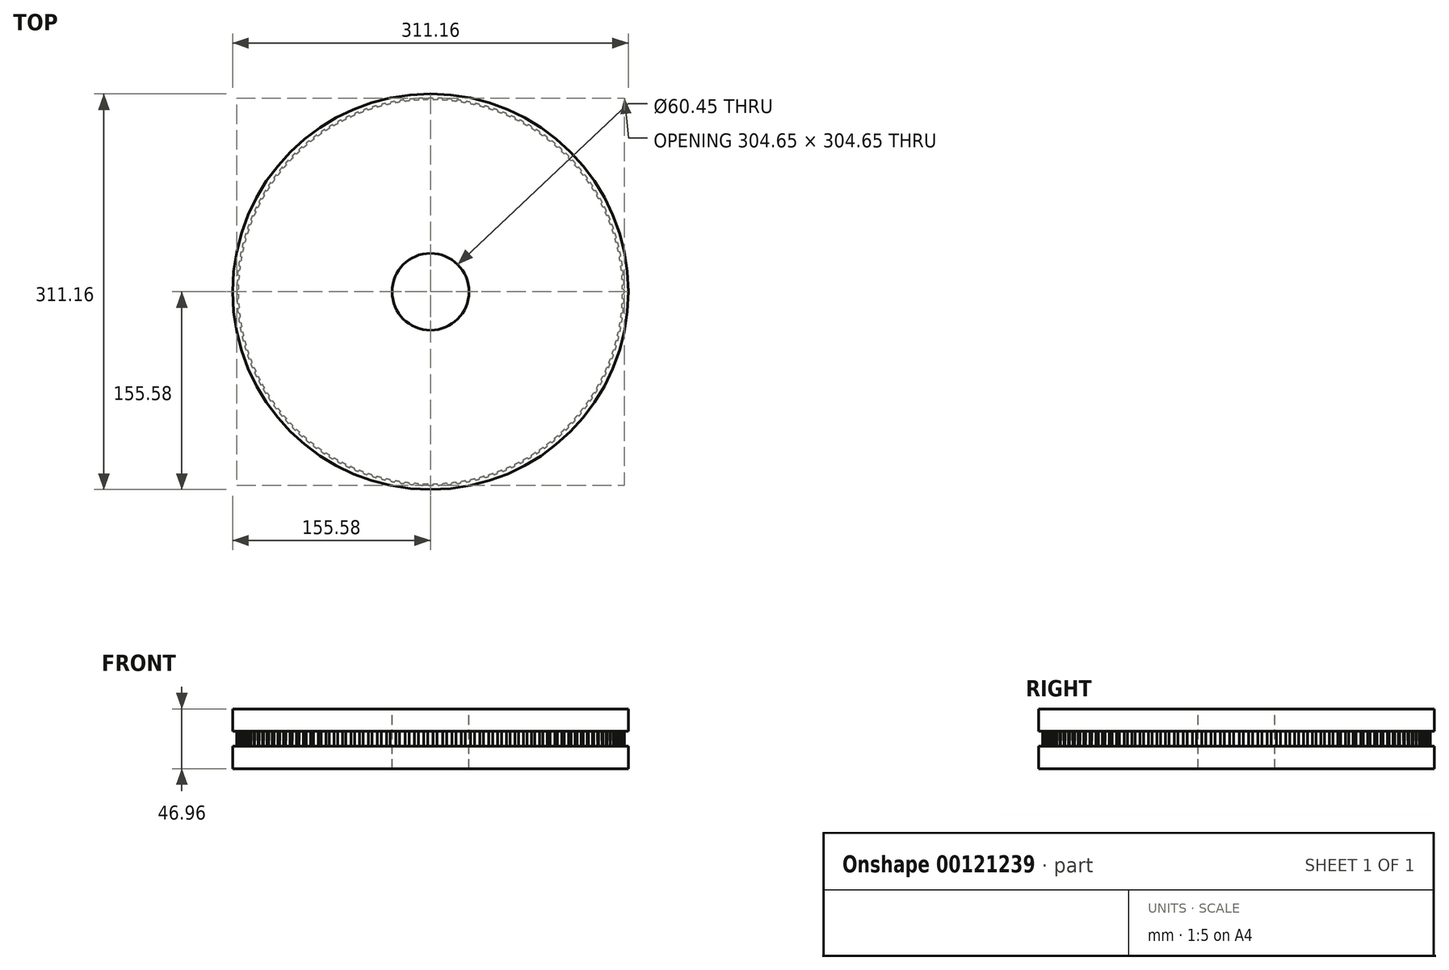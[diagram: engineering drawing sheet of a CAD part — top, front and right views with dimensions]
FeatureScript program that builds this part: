
annotation { "Feature Type Name" : "Feature", "Feature Type Description" : "" }
export const myFeature = defineFeature(function(context is Context, id is Id, definition is map)
    precondition{}
    {
        {
            var Q0;
            Q0=qCreatedBy(makeId("Top.planeOp"),FACE);
            var sketch = newSketch(context, id + "F0", { "sketchPlane" : qUnion([Q0])});
            skCircle(sketch, "E0", {"center": v(0, 0) * mm, "radius": 151 * mm});
            skSolve(sketch);
        }
        {
            var Q0;
            Q0=qSketchRegion(id+"F0",true);
            extrude(context, id + "F1", {"entities" : qUnion([Q0]), "depth" : 11.9 * mm});
        }
        {
            var Q0;
            Q0=qCreatedBy(makeId("Top.planeOp"),FACE);
            var sketch = newSketch(context, id + "F2", { "sketchPlane" : qUnion([Q0])});
            skLineSegment(sketch, "E1", {"start": v(0, -0.08) * mm, "end": v(0, 183.08) * mm, "construction": true});
            skArc(sketch, "E2", {"start": v(1.26, 152.32) * mm, "mid": v(0, 152.32) * mm, "end": v(-1.26, 152.32) * mm});
            skLineSegment(sketch, "E3", {"start": v(-1.6, 152.1) * mm, "end": v(-2.1, 151.02) * mm});
            skLineSegment(sketch, "E4", {"start": v(1.6, 152.1) * mm, "end": v(2.1, 151.02) * mm});
            skPoint(sketch, "E5.visualSharp", {"position": v(-1.5, 152.32) * mm});
            skArc(sketch, "E5.filletArc", {"start": v(-1.26, 152.32) * mm, "mid": v(-1.46, 152.26) * mm, "end": v(-1.6, 152.1) * mm});
            skPoint(sketch, "E6.visualSharp", {"position": v(1.5, 152.32) * mm});
            skArc(sketch, "E6.filletArc", {"start": v(1.6, 152.1) * mm, "mid": v(1.46, 152.26) * mm, "end": v(1.26, 152.32) * mm});
            skArc(sketch, "E7", {"start": v(-2.27, 150.9) * mm, "mid": v(-2.17, 150.94) * mm, "end": v(-2.1, 151.02) * mm});
            skArc(sketch, "E8", {"start": v(2.1, 151.02) * mm, "mid": v(2.17, 150.94) * mm, "end": v(2.27, 150.9) * mm});
            skPoint(sketch, "E9.orphan", {"position": v(2.15, 150.91) * mm});
            skArc(sketch, "E10", {"start": v(-2.27, 150.9) * mm, "mid": v(0, 150.67) * mm, "end": v(2.27, 150.9) * mm});
            skSolve(sketch);
        }
        {
            var Q0;
            Q0=makeQuery(id+"F2.imprint","IMPRINT",FACE,{"disambiguationData":[TD([[makeQuery(id+"F2.imprint","IMPRINT",EDGE,{"derivedFrom":sQuery(id+"F2.wireOp",EDGE,"E2")}),1.0]])]});
            var Q1;
            Q1=makeQuery(id+"F2.imprint","IMPRINT",FACE,{"disambiguationData":[TD([[makeQuery(id+"F2.imprint","IMPRINT",EDGE,{"derivedFrom":sQuery(id+"F2.wireOp",EDGE,"bbfa1fc5-6552-4957-9194-8f10230bb92c.0")}),1.0]])]});
            var Q2;
            Q2=makeQuery(id+"F1.opExtrude","CAP_FACE",FACE,{"disambiguationData":[OSD([sQuery(id+"F0.wireOp",EDGE,"E0")])],"isStart":false});
            extrude(context, id + "F3", {"entities" : qUnion([Q0, Q1]), "endBound" : BoundingType.UP_TO_SURFACE, "endBoundEntityFace" : qUnion([Q2]), "depth" : 25.4 * mm});
        }
        {
            var Q0;
            Q0=qCreatedBy(makeId("Front.planeOp"),FACE);
            var sketch = newSketch(context, id + "F4", { "sketchPlane" : qUnion([Q0])});
            skLineSegment(sketch, "E11", {"start": v(0, 74.48) * mm, "end": v(0, -67.78) * mm, "construction": true});
            skSolve(sketch);
        }
        {
            var Q0;
            Q0=makeQuery(id+"F3.opExtrude","SWEPT_BODY",BODY,{"disambiguationData":[OSD([sQuery(id+"F2.wireOp",EDGE,"E2"),sQuery(id+"F2.wireOp",EDGE,"E3"),sQuery(id+"F2.wireOp",EDGE,"E4"),sQuery(id+"F2.wireOp",EDGE,"E5.filletArc"),sQuery(id+"F2.wireOp",EDGE,"E6.filletArc"),sQuery(id+"F2.wireOp",EDGE,"E7"),sQuery(id+"F2.wireOp",EDGE,"E8"),sQuery(id+"F2.wireOp",EDGE,"E10")])]});
            var Q1;
            Q1=sQuery(id+"F4.wireOp",EDGE,"E11");
            circularPattern(context, id + "F5", {"entities" : qUnion([Q0]), "axis" : qUnion([Q1]), "angle" : 360 * degree, "instanceCount" : 128, "equalSpace" : true});
        }
        {
            var Q0;
            Q0=makeQuery(id+"F1.opExtrude","SWEPT_BODY",BODY,{"disambiguationData":[OSD([sQuery(id+"F0.wireOp",EDGE,"E0")])]});
            var Q1;
            Q1=makeQuery(id+"F3.opExtrude","SWEPT_BODY",BODY,{"disambiguationData":[OSD([sQuery(id+"F2.wireOp",EDGE,"E2"),sQuery(id+"F2.wireOp",EDGE,"E3"),sQuery(id+"F2.wireOp",EDGE,"E4"),sQuery(id+"F2.wireOp",EDGE,"E5.filletArc"),sQuery(id+"F2.wireOp",EDGE,"E6.filletArc"),sQuery(id+"F2.wireOp",EDGE,"E7"),sQuery(id+"F2.wireOp",EDGE,"E8"),sQuery(id+"F2.wireOp",EDGE,"E10")])]});
            var Q2;
            Q2=makeQuery(id+"F5.opPattern","COPY",BODY,{"derivedFrom":makeQuery(id+"F3.opExtrude","SWEPT_BODY",BODY,{"disambiguationData":[OSD([sQuery(id+"F2.wireOp",EDGE,"E2"),sQuery(id+"F2.wireOp",EDGE,"E3"),sQuery(id+"F2.wireOp",EDGE,"E4"),sQuery(id+"F2.wireOp",EDGE,"E5.filletArc"),sQuery(id+"F2.wireOp",EDGE,"E6.filletArc"),sQuery(id+"F2.wireOp",EDGE,"E7"),sQuery(id+"F2.wireOp",EDGE,"E8"),sQuery(id+"F2.wireOp",EDGE,"E10")])]}),"instanceName":"1"});
            var Q3;
            Q3=makeQuery(id+"F5.opPattern","COPY",BODY,{"derivedFrom":makeQuery(id+"F3.opExtrude","SWEPT_BODY",BODY,{"disambiguationData":[OSD([sQuery(id+"F2.wireOp",EDGE,"E2"),sQuery(id+"F2.wireOp",EDGE,"E3"),sQuery(id+"F2.wireOp",EDGE,"E4"),sQuery(id+"F2.wireOp",EDGE,"E5.filletArc"),sQuery(id+"F2.wireOp",EDGE,"E6.filletArc"),sQuery(id+"F2.wireOp",EDGE,"E7"),sQuery(id+"F2.wireOp",EDGE,"E8"),sQuery(id+"F2.wireOp",EDGE,"E10")])]}),"instanceName":"2"});
            var Q4;
            Q4=makeQuery(id+"F5.opPattern","COPY",BODY,{"derivedFrom":makeQuery(id+"F3.opExtrude","SWEPT_BODY",BODY,{"disambiguationData":[OSD([sQuery(id+"F2.wireOp",EDGE,"E2"),sQuery(id+"F2.wireOp",EDGE,"E3"),sQuery(id+"F2.wireOp",EDGE,"E4"),sQuery(id+"F2.wireOp",EDGE,"E5.filletArc"),sQuery(id+"F2.wireOp",EDGE,"E6.filletArc"),sQuery(id+"F2.wireOp",EDGE,"E7"),sQuery(id+"F2.wireOp",EDGE,"E8"),sQuery(id+"F2.wireOp",EDGE,"E10")])]}),"instanceName":"3"});
            var Q5;
            Q5=makeQuery(id+"F5.opPattern","COPY",BODY,{"derivedFrom":makeQuery(id+"F3.opExtrude","SWEPT_BODY",BODY,{"disambiguationData":[OSD([sQuery(id+"F2.wireOp",EDGE,"E2"),sQuery(id+"F2.wireOp",EDGE,"E3"),sQuery(id+"F2.wireOp",EDGE,"E4"),sQuery(id+"F2.wireOp",EDGE,"E5.filletArc"),sQuery(id+"F2.wireOp",EDGE,"E6.filletArc"),sQuery(id+"F2.wireOp",EDGE,"E7"),sQuery(id+"F2.wireOp",EDGE,"E8"),sQuery(id+"F2.wireOp",EDGE,"E10")])]}),"instanceName":"4"});
            var Q6;
            Q6=makeQuery(id+"F5.opPattern","COPY",BODY,{"derivedFrom":makeQuery(id+"F3.opExtrude","SWEPT_BODY",BODY,{"disambiguationData":[OSD([sQuery(id+"F2.wireOp",EDGE,"E2"),sQuery(id+"F2.wireOp",EDGE,"E3"),sQuery(id+"F2.wireOp",EDGE,"E4"),sQuery(id+"F2.wireOp",EDGE,"E5.filletArc"),sQuery(id+"F2.wireOp",EDGE,"E6.filletArc"),sQuery(id+"F2.wireOp",EDGE,"E7"),sQuery(id+"F2.wireOp",EDGE,"E8"),sQuery(id+"F2.wireOp",EDGE,"E10")])]}),"instanceName":"5"});
            var Q7;
            Q7=makeQuery(id+"F5.opPattern","COPY",BODY,{"derivedFrom":makeQuery(id+"F3.opExtrude","SWEPT_BODY",BODY,{"disambiguationData":[OSD([sQuery(id+"F2.wireOp",EDGE,"E2"),sQuery(id+"F2.wireOp",EDGE,"E3"),sQuery(id+"F2.wireOp",EDGE,"E4"),sQuery(id+"F2.wireOp",EDGE,"E5.filletArc"),sQuery(id+"F2.wireOp",EDGE,"E6.filletArc"),sQuery(id+"F2.wireOp",EDGE,"E7"),sQuery(id+"F2.wireOp",EDGE,"E8"),sQuery(id+"F2.wireOp",EDGE,"E10")])]}),"instanceName":"6"});
            var Q8;
            Q8=makeQuery(id+"F5.opPattern","COPY",BODY,{"derivedFrom":makeQuery(id+"F3.opExtrude","SWEPT_BODY",BODY,{"disambiguationData":[OSD([sQuery(id+"F2.wireOp",EDGE,"E2"),sQuery(id+"F2.wireOp",EDGE,"E3"),sQuery(id+"F2.wireOp",EDGE,"E4"),sQuery(id+"F2.wireOp",EDGE,"E5.filletArc"),sQuery(id+"F2.wireOp",EDGE,"E6.filletArc"),sQuery(id+"F2.wireOp",EDGE,"E7"),sQuery(id+"F2.wireOp",EDGE,"E8"),sQuery(id+"F2.wireOp",EDGE,"E10")])]}),"instanceName":"7"});
            var Q9;
            Q9=makeQuery(id+"F5.opPattern","COPY",BODY,{"derivedFrom":makeQuery(id+"F3.opExtrude","SWEPT_BODY",BODY,{"disambiguationData":[OSD([sQuery(id+"F2.wireOp",EDGE,"E2"),sQuery(id+"F2.wireOp",EDGE,"E3"),sQuery(id+"F2.wireOp",EDGE,"E4"),sQuery(id+"F2.wireOp",EDGE,"E5.filletArc"),sQuery(id+"F2.wireOp",EDGE,"E6.filletArc"),sQuery(id+"F2.wireOp",EDGE,"E7"),sQuery(id+"F2.wireOp",EDGE,"E8"),sQuery(id+"F2.wireOp",EDGE,"E10")])]}),"instanceName":"8"});
            var Q10;
            Q10=makeQuery(id+"F5.opPattern","COPY",BODY,{"derivedFrom":makeQuery(id+"F3.opExtrude","SWEPT_BODY",BODY,{"disambiguationData":[OSD([sQuery(id+"F2.wireOp",EDGE,"E2"),sQuery(id+"F2.wireOp",EDGE,"E3"),sQuery(id+"F2.wireOp",EDGE,"E4"),sQuery(id+"F2.wireOp",EDGE,"E5.filletArc"),sQuery(id+"F2.wireOp",EDGE,"E6.filletArc"),sQuery(id+"F2.wireOp",EDGE,"E7"),sQuery(id+"F2.wireOp",EDGE,"E8"),sQuery(id+"F2.wireOp",EDGE,"E10")])]}),"instanceName":"9"});
            var Q11;
            Q11=makeQuery(id+"F5.opPattern","COPY",BODY,{"derivedFrom":makeQuery(id+"F3.opExtrude","SWEPT_BODY",BODY,{"disambiguationData":[OSD([sQuery(id+"F2.wireOp",EDGE,"E2"),sQuery(id+"F2.wireOp",EDGE,"E3"),sQuery(id+"F2.wireOp",EDGE,"E4"),sQuery(id+"F2.wireOp",EDGE,"E5.filletArc"),sQuery(id+"F2.wireOp",EDGE,"E6.filletArc"),sQuery(id+"F2.wireOp",EDGE,"E7"),sQuery(id+"F2.wireOp",EDGE,"E8"),sQuery(id+"F2.wireOp",EDGE,"E10")])]}),"instanceName":"10"});
            var Q12;
            Q12=makeQuery(id+"F5.opPattern","COPY",BODY,{"derivedFrom":makeQuery(id+"F3.opExtrude","SWEPT_BODY",BODY,{"disambiguationData":[OSD([sQuery(id+"F2.wireOp",EDGE,"E2"),sQuery(id+"F2.wireOp",EDGE,"E3"),sQuery(id+"F2.wireOp",EDGE,"E4"),sQuery(id+"F2.wireOp",EDGE,"E5.filletArc"),sQuery(id+"F2.wireOp",EDGE,"E6.filletArc"),sQuery(id+"F2.wireOp",EDGE,"E7"),sQuery(id+"F2.wireOp",EDGE,"E8"),sQuery(id+"F2.wireOp",EDGE,"E10")])]}),"instanceName":"11"});
            var Q13;
            Q13=makeQuery(id+"F5.opPattern","COPY",BODY,{"derivedFrom":makeQuery(id+"F3.opExtrude","SWEPT_BODY",BODY,{"disambiguationData":[OSD([sQuery(id+"F2.wireOp",EDGE,"E2"),sQuery(id+"F2.wireOp",EDGE,"E3"),sQuery(id+"F2.wireOp",EDGE,"E4"),sQuery(id+"F2.wireOp",EDGE,"E5.filletArc"),sQuery(id+"F2.wireOp",EDGE,"E6.filletArc"),sQuery(id+"F2.wireOp",EDGE,"E7"),sQuery(id+"F2.wireOp",EDGE,"E8"),sQuery(id+"F2.wireOp",EDGE,"E10")])]}),"instanceName":"12"});
            var Q14;
            Q14=makeQuery(id+"F5.opPattern","COPY",BODY,{"derivedFrom":makeQuery(id+"F3.opExtrude","SWEPT_BODY",BODY,{"disambiguationData":[OSD([sQuery(id+"F2.wireOp",EDGE,"E2"),sQuery(id+"F2.wireOp",EDGE,"E3"),sQuery(id+"F2.wireOp",EDGE,"E4"),sQuery(id+"F2.wireOp",EDGE,"E5.filletArc"),sQuery(id+"F2.wireOp",EDGE,"E6.filletArc"),sQuery(id+"F2.wireOp",EDGE,"E7"),sQuery(id+"F2.wireOp",EDGE,"E8"),sQuery(id+"F2.wireOp",EDGE,"E10")])]}),"instanceName":"13"});
            var Q15;
            Q15=makeQuery(id+"F5.opPattern","COPY",BODY,{"derivedFrom":makeQuery(id+"F3.opExtrude","SWEPT_BODY",BODY,{"disambiguationData":[OSD([sQuery(id+"F2.wireOp",EDGE,"E2"),sQuery(id+"F2.wireOp",EDGE,"E3"),sQuery(id+"F2.wireOp",EDGE,"E4"),sQuery(id+"F2.wireOp",EDGE,"E5.filletArc"),sQuery(id+"F2.wireOp",EDGE,"E6.filletArc"),sQuery(id+"F2.wireOp",EDGE,"E7"),sQuery(id+"F2.wireOp",EDGE,"E8"),sQuery(id+"F2.wireOp",EDGE,"E10")])]}),"instanceName":"14"});
            var Q16;
            Q16=makeQuery(id+"F5.opPattern","COPY",BODY,{"derivedFrom":makeQuery(id+"F3.opExtrude","SWEPT_BODY",BODY,{"disambiguationData":[OSD([sQuery(id+"F2.wireOp",EDGE,"E2"),sQuery(id+"F2.wireOp",EDGE,"E3"),sQuery(id+"F2.wireOp",EDGE,"E4"),sQuery(id+"F2.wireOp",EDGE,"E5.filletArc"),sQuery(id+"F2.wireOp",EDGE,"E6.filletArc"),sQuery(id+"F2.wireOp",EDGE,"E7"),sQuery(id+"F2.wireOp",EDGE,"E8"),sQuery(id+"F2.wireOp",EDGE,"E10")])]}),"instanceName":"15"});
            var Q17;
            Q17=makeQuery(id+"F5.opPattern","COPY",BODY,{"derivedFrom":makeQuery(id+"F3.opExtrude","SWEPT_BODY",BODY,{"disambiguationData":[OSD([sQuery(id+"F2.wireOp",EDGE,"E2"),sQuery(id+"F2.wireOp",EDGE,"E3"),sQuery(id+"F2.wireOp",EDGE,"E4"),sQuery(id+"F2.wireOp",EDGE,"E5.filletArc"),sQuery(id+"F2.wireOp",EDGE,"E6.filletArc"),sQuery(id+"F2.wireOp",EDGE,"E7"),sQuery(id+"F2.wireOp",EDGE,"E8"),sQuery(id+"F2.wireOp",EDGE,"E10")])]}),"instanceName":"16"});
            var Q18;
            Q18=makeQuery(id+"F5.opPattern","COPY",BODY,{"derivedFrom":makeQuery(id+"F3.opExtrude","SWEPT_BODY",BODY,{"disambiguationData":[OSD([sQuery(id+"F2.wireOp",EDGE,"E2"),sQuery(id+"F2.wireOp",EDGE,"E3"),sQuery(id+"F2.wireOp",EDGE,"E4"),sQuery(id+"F2.wireOp",EDGE,"E5.filletArc"),sQuery(id+"F2.wireOp",EDGE,"E6.filletArc"),sQuery(id+"F2.wireOp",EDGE,"E7"),sQuery(id+"F2.wireOp",EDGE,"E8"),sQuery(id+"F2.wireOp",EDGE,"E10")])]}),"instanceName":"17"});
            var Q19;
            Q19=makeQuery(id+"F5.opPattern","COPY",BODY,{"derivedFrom":makeQuery(id+"F3.opExtrude","SWEPT_BODY",BODY,{"disambiguationData":[OSD([sQuery(id+"F2.wireOp",EDGE,"E2"),sQuery(id+"F2.wireOp",EDGE,"E3"),sQuery(id+"F2.wireOp",EDGE,"E4"),sQuery(id+"F2.wireOp",EDGE,"E5.filletArc"),sQuery(id+"F2.wireOp",EDGE,"E6.filletArc"),sQuery(id+"F2.wireOp",EDGE,"E7"),sQuery(id+"F2.wireOp",EDGE,"E8"),sQuery(id+"F2.wireOp",EDGE,"E10")])]}),"instanceName":"18"});
            var Q20;
            Q20=makeQuery(id+"F5.opPattern","COPY",BODY,{"derivedFrom":makeQuery(id+"F3.opExtrude","SWEPT_BODY",BODY,{"disambiguationData":[OSD([sQuery(id+"F2.wireOp",EDGE,"E2"),sQuery(id+"F2.wireOp",EDGE,"E3"),sQuery(id+"F2.wireOp",EDGE,"E4"),sQuery(id+"F2.wireOp",EDGE,"E5.filletArc"),sQuery(id+"F2.wireOp",EDGE,"E6.filletArc"),sQuery(id+"F2.wireOp",EDGE,"E7"),sQuery(id+"F2.wireOp",EDGE,"E8"),sQuery(id+"F2.wireOp",EDGE,"E10")])]}),"instanceName":"19"});
            var Q21;
            Q21=makeQuery(id+"F5.opPattern","COPY",BODY,{"derivedFrom":makeQuery(id+"F3.opExtrude","SWEPT_BODY",BODY,{"disambiguationData":[OSD([sQuery(id+"F2.wireOp",EDGE,"E2"),sQuery(id+"F2.wireOp",EDGE,"E3"),sQuery(id+"F2.wireOp",EDGE,"E4"),sQuery(id+"F2.wireOp",EDGE,"E5.filletArc"),sQuery(id+"F2.wireOp",EDGE,"E6.filletArc"),sQuery(id+"F2.wireOp",EDGE,"E7"),sQuery(id+"F2.wireOp",EDGE,"E8"),sQuery(id+"F2.wireOp",EDGE,"E10")])]}),"instanceName":"20"});
            var Q22;
            Q22=makeQuery(id+"F5.opPattern","COPY",BODY,{"derivedFrom":makeQuery(id+"F3.opExtrude","SWEPT_BODY",BODY,{"disambiguationData":[OSD([sQuery(id+"F2.wireOp",EDGE,"E2"),sQuery(id+"F2.wireOp",EDGE,"E3"),sQuery(id+"F2.wireOp",EDGE,"E4"),sQuery(id+"F2.wireOp",EDGE,"E5.filletArc"),sQuery(id+"F2.wireOp",EDGE,"E6.filletArc"),sQuery(id+"F2.wireOp",EDGE,"E7"),sQuery(id+"F2.wireOp",EDGE,"E8"),sQuery(id+"F2.wireOp",EDGE,"E10")])]}),"instanceName":"21"});
            var Q23;
            Q23=makeQuery(id+"F5.opPattern","COPY",BODY,{"derivedFrom":makeQuery(id+"F3.opExtrude","SWEPT_BODY",BODY,{"disambiguationData":[OSD([sQuery(id+"F2.wireOp",EDGE,"E2"),sQuery(id+"F2.wireOp",EDGE,"E3"),sQuery(id+"F2.wireOp",EDGE,"E4"),sQuery(id+"F2.wireOp",EDGE,"E5.filletArc"),sQuery(id+"F2.wireOp",EDGE,"E6.filletArc"),sQuery(id+"F2.wireOp",EDGE,"E7"),sQuery(id+"F2.wireOp",EDGE,"E8"),sQuery(id+"F2.wireOp",EDGE,"E10")])]}),"instanceName":"22"});
            var Q24;
            Q24=makeQuery(id+"F5.opPattern","COPY",BODY,{"derivedFrom":makeQuery(id+"F3.opExtrude","SWEPT_BODY",BODY,{"disambiguationData":[OSD([sQuery(id+"F2.wireOp",EDGE,"E2"),sQuery(id+"F2.wireOp",EDGE,"E3"),sQuery(id+"F2.wireOp",EDGE,"E4"),sQuery(id+"F2.wireOp",EDGE,"E5.filletArc"),sQuery(id+"F2.wireOp",EDGE,"E6.filletArc"),sQuery(id+"F2.wireOp",EDGE,"E7"),sQuery(id+"F2.wireOp",EDGE,"E8"),sQuery(id+"F2.wireOp",EDGE,"E10")])]}),"instanceName":"23"});
            var Q25;
            Q25=makeQuery(id+"F5.opPattern","COPY",BODY,{"derivedFrom":makeQuery(id+"F3.opExtrude","SWEPT_BODY",BODY,{"disambiguationData":[OSD([sQuery(id+"F2.wireOp",EDGE,"E2"),sQuery(id+"F2.wireOp",EDGE,"E3"),sQuery(id+"F2.wireOp",EDGE,"E4"),sQuery(id+"F2.wireOp",EDGE,"E5.filletArc"),sQuery(id+"F2.wireOp",EDGE,"E6.filletArc"),sQuery(id+"F2.wireOp",EDGE,"E7"),sQuery(id+"F2.wireOp",EDGE,"E8"),sQuery(id+"F2.wireOp",EDGE,"E10")])]}),"instanceName":"24"});
            var Q26;
            Q26=makeQuery(id+"F5.opPattern","COPY",BODY,{"derivedFrom":makeQuery(id+"F3.opExtrude","SWEPT_BODY",BODY,{"disambiguationData":[OSD([sQuery(id+"F2.wireOp",EDGE,"E2"),sQuery(id+"F2.wireOp",EDGE,"E3"),sQuery(id+"F2.wireOp",EDGE,"E4"),sQuery(id+"F2.wireOp",EDGE,"E5.filletArc"),sQuery(id+"F2.wireOp",EDGE,"E6.filletArc"),sQuery(id+"F2.wireOp",EDGE,"E7"),sQuery(id+"F2.wireOp",EDGE,"E8"),sQuery(id+"F2.wireOp",EDGE,"E10")])]}),"instanceName":"25"});
            var Q27;
            Q27=makeQuery(id+"F5.opPattern","COPY",BODY,{"derivedFrom":makeQuery(id+"F3.opExtrude","SWEPT_BODY",BODY,{"disambiguationData":[OSD([sQuery(id+"F2.wireOp",EDGE,"E2"),sQuery(id+"F2.wireOp",EDGE,"E3"),sQuery(id+"F2.wireOp",EDGE,"E4"),sQuery(id+"F2.wireOp",EDGE,"E5.filletArc"),sQuery(id+"F2.wireOp",EDGE,"E6.filletArc"),sQuery(id+"F2.wireOp",EDGE,"E7"),sQuery(id+"F2.wireOp",EDGE,"E8"),sQuery(id+"F2.wireOp",EDGE,"E10")])]}),"instanceName":"26"});
            var Q28;
            Q28=makeQuery(id+"F5.opPattern","COPY",BODY,{"derivedFrom":makeQuery(id+"F3.opExtrude","SWEPT_BODY",BODY,{"disambiguationData":[OSD([sQuery(id+"F2.wireOp",EDGE,"E2"),sQuery(id+"F2.wireOp",EDGE,"E3"),sQuery(id+"F2.wireOp",EDGE,"E4"),sQuery(id+"F2.wireOp",EDGE,"E5.filletArc"),sQuery(id+"F2.wireOp",EDGE,"E6.filletArc"),sQuery(id+"F2.wireOp",EDGE,"E7"),sQuery(id+"F2.wireOp",EDGE,"E8"),sQuery(id+"F2.wireOp",EDGE,"E10")])]}),"instanceName":"27"});
            var Q29;
            Q29=makeQuery(id+"F5.opPattern","COPY",BODY,{"derivedFrom":makeQuery(id+"F3.opExtrude","SWEPT_BODY",BODY,{"disambiguationData":[OSD([sQuery(id+"F2.wireOp",EDGE,"E2"),sQuery(id+"F2.wireOp",EDGE,"E3"),sQuery(id+"F2.wireOp",EDGE,"E4"),sQuery(id+"F2.wireOp",EDGE,"E5.filletArc"),sQuery(id+"F2.wireOp",EDGE,"E6.filletArc"),sQuery(id+"F2.wireOp",EDGE,"E7"),sQuery(id+"F2.wireOp",EDGE,"E8"),sQuery(id+"F2.wireOp",EDGE,"E10")])]}),"instanceName":"28"});
            var Q30;
            Q30=makeQuery(id+"F5.opPattern","COPY",BODY,{"derivedFrom":makeQuery(id+"F3.opExtrude","SWEPT_BODY",BODY,{"disambiguationData":[OSD([sQuery(id+"F2.wireOp",EDGE,"E2"),sQuery(id+"F2.wireOp",EDGE,"E3"),sQuery(id+"F2.wireOp",EDGE,"E4"),sQuery(id+"F2.wireOp",EDGE,"E5.filletArc"),sQuery(id+"F2.wireOp",EDGE,"E6.filletArc"),sQuery(id+"F2.wireOp",EDGE,"E7"),sQuery(id+"F2.wireOp",EDGE,"E8"),sQuery(id+"F2.wireOp",EDGE,"E10")])]}),"instanceName":"29"});
            var Q31;
            Q31=makeQuery(id+"F5.opPattern","COPY",BODY,{"derivedFrom":makeQuery(id+"F3.opExtrude","SWEPT_BODY",BODY,{"disambiguationData":[OSD([sQuery(id+"F2.wireOp",EDGE,"E2"),sQuery(id+"F2.wireOp",EDGE,"E3"),sQuery(id+"F2.wireOp",EDGE,"E4"),sQuery(id+"F2.wireOp",EDGE,"E5.filletArc"),sQuery(id+"F2.wireOp",EDGE,"E6.filletArc"),sQuery(id+"F2.wireOp",EDGE,"E7"),sQuery(id+"F2.wireOp",EDGE,"E8"),sQuery(id+"F2.wireOp",EDGE,"E10")])]}),"instanceName":"30"});
            var Q32;
            Q32=makeQuery(id+"F5.opPattern","COPY",BODY,{"derivedFrom":makeQuery(id+"F3.opExtrude","SWEPT_BODY",BODY,{"disambiguationData":[OSD([sQuery(id+"F2.wireOp",EDGE,"E2"),sQuery(id+"F2.wireOp",EDGE,"E3"),sQuery(id+"F2.wireOp",EDGE,"E4"),sQuery(id+"F2.wireOp",EDGE,"E5.filletArc"),sQuery(id+"F2.wireOp",EDGE,"E6.filletArc"),sQuery(id+"F2.wireOp",EDGE,"E7"),sQuery(id+"F2.wireOp",EDGE,"E8"),sQuery(id+"F2.wireOp",EDGE,"E10")])]}),"instanceName":"31"});
            var Q33;
            Q33=makeQuery(id+"F5.opPattern","COPY",BODY,{"derivedFrom":makeQuery(id+"F3.opExtrude","SWEPT_BODY",BODY,{"disambiguationData":[OSD([sQuery(id+"F2.wireOp",EDGE,"E2"),sQuery(id+"F2.wireOp",EDGE,"E3"),sQuery(id+"F2.wireOp",EDGE,"E4"),sQuery(id+"F2.wireOp",EDGE,"E5.filletArc"),sQuery(id+"F2.wireOp",EDGE,"E6.filletArc"),sQuery(id+"F2.wireOp",EDGE,"E7"),sQuery(id+"F2.wireOp",EDGE,"E8"),sQuery(id+"F2.wireOp",EDGE,"E10")])]}),"instanceName":"32"});
            var Q34;
            Q34=makeQuery(id+"F5.opPattern","COPY",BODY,{"derivedFrom":makeQuery(id+"F3.opExtrude","SWEPT_BODY",BODY,{"disambiguationData":[OSD([sQuery(id+"F2.wireOp",EDGE,"E2"),sQuery(id+"F2.wireOp",EDGE,"E3"),sQuery(id+"F2.wireOp",EDGE,"E4"),sQuery(id+"F2.wireOp",EDGE,"E5.filletArc"),sQuery(id+"F2.wireOp",EDGE,"E6.filletArc"),sQuery(id+"F2.wireOp",EDGE,"E7"),sQuery(id+"F2.wireOp",EDGE,"E8"),sQuery(id+"F2.wireOp",EDGE,"E10")])]}),"instanceName":"33"});
            var Q35;
            Q35=makeQuery(id+"F5.opPattern","COPY",BODY,{"derivedFrom":makeQuery(id+"F3.opExtrude","SWEPT_BODY",BODY,{"disambiguationData":[OSD([sQuery(id+"F2.wireOp",EDGE,"E2"),sQuery(id+"F2.wireOp",EDGE,"E3"),sQuery(id+"F2.wireOp",EDGE,"E4"),sQuery(id+"F2.wireOp",EDGE,"E5.filletArc"),sQuery(id+"F2.wireOp",EDGE,"E6.filletArc"),sQuery(id+"F2.wireOp",EDGE,"E7"),sQuery(id+"F2.wireOp",EDGE,"E8"),sQuery(id+"F2.wireOp",EDGE,"E10")])]}),"instanceName":"34"});
            var Q36;
            Q36=makeQuery(id+"F5.opPattern","COPY",BODY,{"derivedFrom":makeQuery(id+"F3.opExtrude","SWEPT_BODY",BODY,{"disambiguationData":[OSD([sQuery(id+"F2.wireOp",EDGE,"E2"),sQuery(id+"F2.wireOp",EDGE,"E3"),sQuery(id+"F2.wireOp",EDGE,"E4"),sQuery(id+"F2.wireOp",EDGE,"E5.filletArc"),sQuery(id+"F2.wireOp",EDGE,"E6.filletArc"),sQuery(id+"F2.wireOp",EDGE,"E7"),sQuery(id+"F2.wireOp",EDGE,"E8"),sQuery(id+"F2.wireOp",EDGE,"E10")])]}),"instanceName":"35"});
            var Q37;
            Q37=makeQuery(id+"F5.opPattern","COPY",BODY,{"derivedFrom":makeQuery(id+"F3.opExtrude","SWEPT_BODY",BODY,{"disambiguationData":[OSD([sQuery(id+"F2.wireOp",EDGE,"E2"),sQuery(id+"F2.wireOp",EDGE,"E3"),sQuery(id+"F2.wireOp",EDGE,"E4"),sQuery(id+"F2.wireOp",EDGE,"E5.filletArc"),sQuery(id+"F2.wireOp",EDGE,"E6.filletArc"),sQuery(id+"F2.wireOp",EDGE,"E7"),sQuery(id+"F2.wireOp",EDGE,"E8"),sQuery(id+"F2.wireOp",EDGE,"E10")])]}),"instanceName":"36"});
            var Q38;
            Q38=makeQuery(id+"F5.opPattern","COPY",BODY,{"derivedFrom":makeQuery(id+"F3.opExtrude","SWEPT_BODY",BODY,{"disambiguationData":[OSD([sQuery(id+"F2.wireOp",EDGE,"E2"),sQuery(id+"F2.wireOp",EDGE,"E3"),sQuery(id+"F2.wireOp",EDGE,"E4"),sQuery(id+"F2.wireOp",EDGE,"E5.filletArc"),sQuery(id+"F2.wireOp",EDGE,"E6.filletArc"),sQuery(id+"F2.wireOp",EDGE,"E7"),sQuery(id+"F2.wireOp",EDGE,"E8"),sQuery(id+"F2.wireOp",EDGE,"E10")])]}),"instanceName":"37"});
            var Q39;
            Q39=makeQuery(id+"F5.opPattern","COPY",BODY,{"derivedFrom":makeQuery(id+"F3.opExtrude","SWEPT_BODY",BODY,{"disambiguationData":[OSD([sQuery(id+"F2.wireOp",EDGE,"E2"),sQuery(id+"F2.wireOp",EDGE,"E3"),sQuery(id+"F2.wireOp",EDGE,"E4"),sQuery(id+"F2.wireOp",EDGE,"E5.filletArc"),sQuery(id+"F2.wireOp",EDGE,"E6.filletArc"),sQuery(id+"F2.wireOp",EDGE,"E7"),sQuery(id+"F2.wireOp",EDGE,"E8"),sQuery(id+"F2.wireOp",EDGE,"E10")])]}),"instanceName":"38"});
            var Q40;
            Q40=makeQuery(id+"F5.opPattern","COPY",BODY,{"derivedFrom":makeQuery(id+"F3.opExtrude","SWEPT_BODY",BODY,{"disambiguationData":[OSD([sQuery(id+"F2.wireOp",EDGE,"E2"),sQuery(id+"F2.wireOp",EDGE,"E3"),sQuery(id+"F2.wireOp",EDGE,"E4"),sQuery(id+"F2.wireOp",EDGE,"E5.filletArc"),sQuery(id+"F2.wireOp",EDGE,"E6.filletArc"),sQuery(id+"F2.wireOp",EDGE,"E7"),sQuery(id+"F2.wireOp",EDGE,"E8"),sQuery(id+"F2.wireOp",EDGE,"E10")])]}),"instanceName":"39"});
            var Q41;
            Q41=makeQuery(id+"F5.opPattern","COPY",BODY,{"derivedFrom":makeQuery(id+"F3.opExtrude","SWEPT_BODY",BODY,{"disambiguationData":[OSD([sQuery(id+"F2.wireOp",EDGE,"E2"),sQuery(id+"F2.wireOp",EDGE,"E3"),sQuery(id+"F2.wireOp",EDGE,"E4"),sQuery(id+"F2.wireOp",EDGE,"E5.filletArc"),sQuery(id+"F2.wireOp",EDGE,"E6.filletArc"),sQuery(id+"F2.wireOp",EDGE,"E7"),sQuery(id+"F2.wireOp",EDGE,"E8"),sQuery(id+"F2.wireOp",EDGE,"E10")])]}),"instanceName":"40"});
            var Q42;
            Q42=makeQuery(id+"F5.opPattern","COPY",BODY,{"derivedFrom":makeQuery(id+"F3.opExtrude","SWEPT_BODY",BODY,{"disambiguationData":[OSD([sQuery(id+"F2.wireOp",EDGE,"E2"),sQuery(id+"F2.wireOp",EDGE,"E3"),sQuery(id+"F2.wireOp",EDGE,"E4"),sQuery(id+"F2.wireOp",EDGE,"E5.filletArc"),sQuery(id+"F2.wireOp",EDGE,"E6.filletArc"),sQuery(id+"F2.wireOp",EDGE,"E7"),sQuery(id+"F2.wireOp",EDGE,"E8"),sQuery(id+"F2.wireOp",EDGE,"E10")])]}),"instanceName":"41"});
            var Q43;
            Q43=makeQuery(id+"F5.opPattern","COPY",BODY,{"derivedFrom":makeQuery(id+"F3.opExtrude","SWEPT_BODY",BODY,{"disambiguationData":[OSD([sQuery(id+"F2.wireOp",EDGE,"E2"),sQuery(id+"F2.wireOp",EDGE,"E3"),sQuery(id+"F2.wireOp",EDGE,"E4"),sQuery(id+"F2.wireOp",EDGE,"E5.filletArc"),sQuery(id+"F2.wireOp",EDGE,"E6.filletArc"),sQuery(id+"F2.wireOp",EDGE,"E7"),sQuery(id+"F2.wireOp",EDGE,"E8"),sQuery(id+"F2.wireOp",EDGE,"E10")])]}),"instanceName":"42"});
            var Q44;
            Q44=makeQuery(id+"F5.opPattern","COPY",BODY,{"derivedFrom":makeQuery(id+"F3.opExtrude","SWEPT_BODY",BODY,{"disambiguationData":[OSD([sQuery(id+"F2.wireOp",EDGE,"E2"),sQuery(id+"F2.wireOp",EDGE,"E3"),sQuery(id+"F2.wireOp",EDGE,"E4"),sQuery(id+"F2.wireOp",EDGE,"E5.filletArc"),sQuery(id+"F2.wireOp",EDGE,"E6.filletArc"),sQuery(id+"F2.wireOp",EDGE,"E7"),sQuery(id+"F2.wireOp",EDGE,"E8"),sQuery(id+"F2.wireOp",EDGE,"E10")])]}),"instanceName":"43"});
            var Q45;
            Q45=makeQuery(id+"F5.opPattern","COPY",BODY,{"derivedFrom":makeQuery(id+"F3.opExtrude","SWEPT_BODY",BODY,{"disambiguationData":[OSD([sQuery(id+"F2.wireOp",EDGE,"E2"),sQuery(id+"F2.wireOp",EDGE,"E3"),sQuery(id+"F2.wireOp",EDGE,"E4"),sQuery(id+"F2.wireOp",EDGE,"E5.filletArc"),sQuery(id+"F2.wireOp",EDGE,"E6.filletArc"),sQuery(id+"F2.wireOp",EDGE,"E7"),sQuery(id+"F2.wireOp",EDGE,"E8"),sQuery(id+"F2.wireOp",EDGE,"E10")])]}),"instanceName":"44"});
            var Q46;
            Q46=makeQuery(id+"F5.opPattern","COPY",BODY,{"derivedFrom":makeQuery(id+"F3.opExtrude","SWEPT_BODY",BODY,{"disambiguationData":[OSD([sQuery(id+"F2.wireOp",EDGE,"E2"),sQuery(id+"F2.wireOp",EDGE,"E3"),sQuery(id+"F2.wireOp",EDGE,"E4"),sQuery(id+"F2.wireOp",EDGE,"E5.filletArc"),sQuery(id+"F2.wireOp",EDGE,"E6.filletArc"),sQuery(id+"F2.wireOp",EDGE,"E7"),sQuery(id+"F2.wireOp",EDGE,"E8"),sQuery(id+"F2.wireOp",EDGE,"E10")])]}),"instanceName":"45"});
            var Q47;
            Q47=makeQuery(id+"F5.opPattern","COPY",BODY,{"derivedFrom":makeQuery(id+"F3.opExtrude","SWEPT_BODY",BODY,{"disambiguationData":[OSD([sQuery(id+"F2.wireOp",EDGE,"E2"),sQuery(id+"F2.wireOp",EDGE,"E3"),sQuery(id+"F2.wireOp",EDGE,"E4"),sQuery(id+"F2.wireOp",EDGE,"E5.filletArc"),sQuery(id+"F2.wireOp",EDGE,"E6.filletArc"),sQuery(id+"F2.wireOp",EDGE,"E7"),sQuery(id+"F2.wireOp",EDGE,"E8"),sQuery(id+"F2.wireOp",EDGE,"E10")])]}),"instanceName":"46"});
            var Q48;
            Q48=makeQuery(id+"F5.opPattern","COPY",BODY,{"derivedFrom":makeQuery(id+"F3.opExtrude","SWEPT_BODY",BODY,{"disambiguationData":[OSD([sQuery(id+"F2.wireOp",EDGE,"E2"),sQuery(id+"F2.wireOp",EDGE,"E3"),sQuery(id+"F2.wireOp",EDGE,"E4"),sQuery(id+"F2.wireOp",EDGE,"E5.filletArc"),sQuery(id+"F2.wireOp",EDGE,"E6.filletArc"),sQuery(id+"F2.wireOp",EDGE,"E7"),sQuery(id+"F2.wireOp",EDGE,"E8"),sQuery(id+"F2.wireOp",EDGE,"E10")])]}),"instanceName":"47"});
            var Q49;
            Q49=makeQuery(id+"F5.opPattern","COPY",BODY,{"derivedFrom":makeQuery(id+"F3.opExtrude","SWEPT_BODY",BODY,{"disambiguationData":[OSD([sQuery(id+"F2.wireOp",EDGE,"E2"),sQuery(id+"F2.wireOp",EDGE,"E3"),sQuery(id+"F2.wireOp",EDGE,"E4"),sQuery(id+"F2.wireOp",EDGE,"E5.filletArc"),sQuery(id+"F2.wireOp",EDGE,"E6.filletArc"),sQuery(id+"F2.wireOp",EDGE,"E7"),sQuery(id+"F2.wireOp",EDGE,"E8"),sQuery(id+"F2.wireOp",EDGE,"E10")])]}),"instanceName":"48"});
            var Q50;
            Q50=makeQuery(id+"F5.opPattern","COPY",BODY,{"derivedFrom":makeQuery(id+"F3.opExtrude","SWEPT_BODY",BODY,{"disambiguationData":[OSD([sQuery(id+"F2.wireOp",EDGE,"E2"),sQuery(id+"F2.wireOp",EDGE,"E3"),sQuery(id+"F2.wireOp",EDGE,"E4"),sQuery(id+"F2.wireOp",EDGE,"E5.filletArc"),sQuery(id+"F2.wireOp",EDGE,"E6.filletArc"),sQuery(id+"F2.wireOp",EDGE,"E7"),sQuery(id+"F2.wireOp",EDGE,"E8"),sQuery(id+"F2.wireOp",EDGE,"E10")])]}),"instanceName":"49"});
            var Q51;
            Q51=makeQuery(id+"F5.opPattern","COPY",BODY,{"derivedFrom":makeQuery(id+"F3.opExtrude","SWEPT_BODY",BODY,{"disambiguationData":[OSD([sQuery(id+"F2.wireOp",EDGE,"E2"),sQuery(id+"F2.wireOp",EDGE,"E3"),sQuery(id+"F2.wireOp",EDGE,"E4"),sQuery(id+"F2.wireOp",EDGE,"E5.filletArc"),sQuery(id+"F2.wireOp",EDGE,"E6.filletArc"),sQuery(id+"F2.wireOp",EDGE,"E7"),sQuery(id+"F2.wireOp",EDGE,"E8"),sQuery(id+"F2.wireOp",EDGE,"E10")])]}),"instanceName":"50"});
            var Q52;
            Q52=makeQuery(id+"F5.opPattern","COPY",BODY,{"derivedFrom":makeQuery(id+"F3.opExtrude","SWEPT_BODY",BODY,{"disambiguationData":[OSD([sQuery(id+"F2.wireOp",EDGE,"E2"),sQuery(id+"F2.wireOp",EDGE,"E3"),sQuery(id+"F2.wireOp",EDGE,"E4"),sQuery(id+"F2.wireOp",EDGE,"E5.filletArc"),sQuery(id+"F2.wireOp",EDGE,"E6.filletArc"),sQuery(id+"F2.wireOp",EDGE,"E7"),sQuery(id+"F2.wireOp",EDGE,"E8"),sQuery(id+"F2.wireOp",EDGE,"E10")])]}),"instanceName":"51"});
            var Q53;
            Q53=makeQuery(id+"F5.opPattern","COPY",BODY,{"derivedFrom":makeQuery(id+"F3.opExtrude","SWEPT_BODY",BODY,{"disambiguationData":[OSD([sQuery(id+"F2.wireOp",EDGE,"E2"),sQuery(id+"F2.wireOp",EDGE,"E3"),sQuery(id+"F2.wireOp",EDGE,"E4"),sQuery(id+"F2.wireOp",EDGE,"E5.filletArc"),sQuery(id+"F2.wireOp",EDGE,"E6.filletArc"),sQuery(id+"F2.wireOp",EDGE,"E7"),sQuery(id+"F2.wireOp",EDGE,"E8"),sQuery(id+"F2.wireOp",EDGE,"E10")])]}),"instanceName":"52"});
            var Q54;
            Q54=makeQuery(id+"F5.opPattern","COPY",BODY,{"derivedFrom":makeQuery(id+"F3.opExtrude","SWEPT_BODY",BODY,{"disambiguationData":[OSD([sQuery(id+"F2.wireOp",EDGE,"E2"),sQuery(id+"F2.wireOp",EDGE,"E3"),sQuery(id+"F2.wireOp",EDGE,"E4"),sQuery(id+"F2.wireOp",EDGE,"E5.filletArc"),sQuery(id+"F2.wireOp",EDGE,"E6.filletArc"),sQuery(id+"F2.wireOp",EDGE,"E7"),sQuery(id+"F2.wireOp",EDGE,"E8"),sQuery(id+"F2.wireOp",EDGE,"E10")])]}),"instanceName":"53"});
            var Q55;
            Q55=makeQuery(id+"F5.opPattern","COPY",BODY,{"derivedFrom":makeQuery(id+"F3.opExtrude","SWEPT_BODY",BODY,{"disambiguationData":[OSD([sQuery(id+"F2.wireOp",EDGE,"E2"),sQuery(id+"F2.wireOp",EDGE,"E3"),sQuery(id+"F2.wireOp",EDGE,"E4"),sQuery(id+"F2.wireOp",EDGE,"E5.filletArc"),sQuery(id+"F2.wireOp",EDGE,"E6.filletArc"),sQuery(id+"F2.wireOp",EDGE,"E7"),sQuery(id+"F2.wireOp",EDGE,"E8"),sQuery(id+"F2.wireOp",EDGE,"E10")])]}),"instanceName":"54"});
            var Q56;
            Q56=makeQuery(id+"F5.opPattern","COPY",BODY,{"derivedFrom":makeQuery(id+"F3.opExtrude","SWEPT_BODY",BODY,{"disambiguationData":[OSD([sQuery(id+"F2.wireOp",EDGE,"E2"),sQuery(id+"F2.wireOp",EDGE,"E3"),sQuery(id+"F2.wireOp",EDGE,"E4"),sQuery(id+"F2.wireOp",EDGE,"E5.filletArc"),sQuery(id+"F2.wireOp",EDGE,"E6.filletArc"),sQuery(id+"F2.wireOp",EDGE,"E7"),sQuery(id+"F2.wireOp",EDGE,"E8"),sQuery(id+"F2.wireOp",EDGE,"E10")])]}),"instanceName":"55"});
            var Q57;
            Q57=makeQuery(id+"F5.opPattern","COPY",BODY,{"derivedFrom":makeQuery(id+"F3.opExtrude","SWEPT_BODY",BODY,{"disambiguationData":[OSD([sQuery(id+"F2.wireOp",EDGE,"E2"),sQuery(id+"F2.wireOp",EDGE,"E3"),sQuery(id+"F2.wireOp",EDGE,"E4"),sQuery(id+"F2.wireOp",EDGE,"E5.filletArc"),sQuery(id+"F2.wireOp",EDGE,"E6.filletArc"),sQuery(id+"F2.wireOp",EDGE,"E7"),sQuery(id+"F2.wireOp",EDGE,"E8"),sQuery(id+"F2.wireOp",EDGE,"E10")])]}),"instanceName":"56"});
            var Q58;
            Q58=makeQuery(id+"F5.opPattern","COPY",BODY,{"derivedFrom":makeQuery(id+"F3.opExtrude","SWEPT_BODY",BODY,{"disambiguationData":[OSD([sQuery(id+"F2.wireOp",EDGE,"E2"),sQuery(id+"F2.wireOp",EDGE,"E3"),sQuery(id+"F2.wireOp",EDGE,"E4"),sQuery(id+"F2.wireOp",EDGE,"E5.filletArc"),sQuery(id+"F2.wireOp",EDGE,"E6.filletArc"),sQuery(id+"F2.wireOp",EDGE,"E7"),sQuery(id+"F2.wireOp",EDGE,"E8"),sQuery(id+"F2.wireOp",EDGE,"E10")])]}),"instanceName":"57"});
            var Q59;
            Q59=makeQuery(id+"F5.opPattern","COPY",BODY,{"derivedFrom":makeQuery(id+"F3.opExtrude","SWEPT_BODY",BODY,{"disambiguationData":[OSD([sQuery(id+"F2.wireOp",EDGE,"E2"),sQuery(id+"F2.wireOp",EDGE,"E3"),sQuery(id+"F2.wireOp",EDGE,"E4"),sQuery(id+"F2.wireOp",EDGE,"E5.filletArc"),sQuery(id+"F2.wireOp",EDGE,"E6.filletArc"),sQuery(id+"F2.wireOp",EDGE,"E7"),sQuery(id+"F2.wireOp",EDGE,"E8"),sQuery(id+"F2.wireOp",EDGE,"E10")])]}),"instanceName":"58"});
            var Q60;
            Q60=makeQuery(id+"F5.opPattern","COPY",BODY,{"derivedFrom":makeQuery(id+"F3.opExtrude","SWEPT_BODY",BODY,{"disambiguationData":[OSD([sQuery(id+"F2.wireOp",EDGE,"E2"),sQuery(id+"F2.wireOp",EDGE,"E3"),sQuery(id+"F2.wireOp",EDGE,"E4"),sQuery(id+"F2.wireOp",EDGE,"E5.filletArc"),sQuery(id+"F2.wireOp",EDGE,"E6.filletArc"),sQuery(id+"F2.wireOp",EDGE,"E7"),sQuery(id+"F2.wireOp",EDGE,"E8"),sQuery(id+"F2.wireOp",EDGE,"E10")])]}),"instanceName":"59"});
            var Q61;
            Q61=makeQuery(id+"F5.opPattern","COPY",BODY,{"derivedFrom":makeQuery(id+"F3.opExtrude","SWEPT_BODY",BODY,{"disambiguationData":[OSD([sQuery(id+"F2.wireOp",EDGE,"E2"),sQuery(id+"F2.wireOp",EDGE,"E3"),sQuery(id+"F2.wireOp",EDGE,"E4"),sQuery(id+"F2.wireOp",EDGE,"E5.filletArc"),sQuery(id+"F2.wireOp",EDGE,"E6.filletArc"),sQuery(id+"F2.wireOp",EDGE,"E7"),sQuery(id+"F2.wireOp",EDGE,"E8"),sQuery(id+"F2.wireOp",EDGE,"E10")])]}),"instanceName":"60"});
            var Q62;
            Q62=makeQuery(id+"F5.opPattern","COPY",BODY,{"derivedFrom":makeQuery(id+"F3.opExtrude","SWEPT_BODY",BODY,{"disambiguationData":[OSD([sQuery(id+"F2.wireOp",EDGE,"E2"),sQuery(id+"F2.wireOp",EDGE,"E3"),sQuery(id+"F2.wireOp",EDGE,"E4"),sQuery(id+"F2.wireOp",EDGE,"E5.filletArc"),sQuery(id+"F2.wireOp",EDGE,"E6.filletArc"),sQuery(id+"F2.wireOp",EDGE,"E7"),sQuery(id+"F2.wireOp",EDGE,"E8"),sQuery(id+"F2.wireOp",EDGE,"E10")])]}),"instanceName":"61"});
            var Q63;
            Q63=makeQuery(id+"F5.opPattern","COPY",BODY,{"derivedFrom":makeQuery(id+"F3.opExtrude","SWEPT_BODY",BODY,{"disambiguationData":[OSD([sQuery(id+"F2.wireOp",EDGE,"E2"),sQuery(id+"F2.wireOp",EDGE,"E3"),sQuery(id+"F2.wireOp",EDGE,"E4"),sQuery(id+"F2.wireOp",EDGE,"E5.filletArc"),sQuery(id+"F2.wireOp",EDGE,"E6.filletArc"),sQuery(id+"F2.wireOp",EDGE,"E7"),sQuery(id+"F2.wireOp",EDGE,"E8"),sQuery(id+"F2.wireOp",EDGE,"E10")])]}),"instanceName":"62"});
            var Q64;
            Q64=makeQuery(id+"F5.opPattern","COPY",BODY,{"derivedFrom":makeQuery(id+"F3.opExtrude","SWEPT_BODY",BODY,{"disambiguationData":[OSD([sQuery(id+"F2.wireOp",EDGE,"E2"),sQuery(id+"F2.wireOp",EDGE,"E3"),sQuery(id+"F2.wireOp",EDGE,"E4"),sQuery(id+"F2.wireOp",EDGE,"E5.filletArc"),sQuery(id+"F2.wireOp",EDGE,"E6.filletArc"),sQuery(id+"F2.wireOp",EDGE,"E7"),sQuery(id+"F2.wireOp",EDGE,"E8"),sQuery(id+"F2.wireOp",EDGE,"E10")])]}),"instanceName":"63"});
            var Q65;
            Q65=makeQuery(id+"F5.opPattern","COPY",BODY,{"derivedFrom":makeQuery(id+"F3.opExtrude","SWEPT_BODY",BODY,{"disambiguationData":[OSD([sQuery(id+"F2.wireOp",EDGE,"E2"),sQuery(id+"F2.wireOp",EDGE,"E3"),sQuery(id+"F2.wireOp",EDGE,"E4"),sQuery(id+"F2.wireOp",EDGE,"E5.filletArc"),sQuery(id+"F2.wireOp",EDGE,"E6.filletArc"),sQuery(id+"F2.wireOp",EDGE,"E7"),sQuery(id+"F2.wireOp",EDGE,"E8"),sQuery(id+"F2.wireOp",EDGE,"E10")])]}),"instanceName":"64"});
            var Q66;
            Q66=makeQuery(id+"F5.opPattern","COPY",BODY,{"derivedFrom":makeQuery(id+"F3.opExtrude","SWEPT_BODY",BODY,{"disambiguationData":[OSD([sQuery(id+"F2.wireOp",EDGE,"E2"),sQuery(id+"F2.wireOp",EDGE,"E3"),sQuery(id+"F2.wireOp",EDGE,"E4"),sQuery(id+"F2.wireOp",EDGE,"E5.filletArc"),sQuery(id+"F2.wireOp",EDGE,"E6.filletArc"),sQuery(id+"F2.wireOp",EDGE,"E7"),sQuery(id+"F2.wireOp",EDGE,"E8"),sQuery(id+"F2.wireOp",EDGE,"E10")])]}),"instanceName":"65"});
            var Q67;
            Q67=makeQuery(id+"F5.opPattern","COPY",BODY,{"derivedFrom":makeQuery(id+"F3.opExtrude","SWEPT_BODY",BODY,{"disambiguationData":[OSD([sQuery(id+"F2.wireOp",EDGE,"E2"),sQuery(id+"F2.wireOp",EDGE,"E3"),sQuery(id+"F2.wireOp",EDGE,"E4"),sQuery(id+"F2.wireOp",EDGE,"E5.filletArc"),sQuery(id+"F2.wireOp",EDGE,"E6.filletArc"),sQuery(id+"F2.wireOp",EDGE,"E7"),sQuery(id+"F2.wireOp",EDGE,"E8"),sQuery(id+"F2.wireOp",EDGE,"E10")])]}),"instanceName":"66"});
            var Q68;
            Q68=makeQuery(id+"F5.opPattern","COPY",BODY,{"derivedFrom":makeQuery(id+"F3.opExtrude","SWEPT_BODY",BODY,{"disambiguationData":[OSD([sQuery(id+"F2.wireOp",EDGE,"E2"),sQuery(id+"F2.wireOp",EDGE,"E3"),sQuery(id+"F2.wireOp",EDGE,"E4"),sQuery(id+"F2.wireOp",EDGE,"E5.filletArc"),sQuery(id+"F2.wireOp",EDGE,"E6.filletArc"),sQuery(id+"F2.wireOp",EDGE,"E7"),sQuery(id+"F2.wireOp",EDGE,"E8"),sQuery(id+"F2.wireOp",EDGE,"E10")])]}),"instanceName":"67"});
            var Q69;
            Q69=makeQuery(id+"F5.opPattern","COPY",BODY,{"derivedFrom":makeQuery(id+"F3.opExtrude","SWEPT_BODY",BODY,{"disambiguationData":[OSD([sQuery(id+"F2.wireOp",EDGE,"E2"),sQuery(id+"F2.wireOp",EDGE,"E3"),sQuery(id+"F2.wireOp",EDGE,"E4"),sQuery(id+"F2.wireOp",EDGE,"E5.filletArc"),sQuery(id+"F2.wireOp",EDGE,"E6.filletArc"),sQuery(id+"F2.wireOp",EDGE,"E7"),sQuery(id+"F2.wireOp",EDGE,"E8"),sQuery(id+"F2.wireOp",EDGE,"E10")])]}),"instanceName":"68"});
            var Q70;
            Q70=makeQuery(id+"F5.opPattern","COPY",BODY,{"derivedFrom":makeQuery(id+"F3.opExtrude","SWEPT_BODY",BODY,{"disambiguationData":[OSD([sQuery(id+"F2.wireOp",EDGE,"E2"),sQuery(id+"F2.wireOp",EDGE,"E3"),sQuery(id+"F2.wireOp",EDGE,"E4"),sQuery(id+"F2.wireOp",EDGE,"E5.filletArc"),sQuery(id+"F2.wireOp",EDGE,"E6.filletArc"),sQuery(id+"F2.wireOp",EDGE,"E7"),sQuery(id+"F2.wireOp",EDGE,"E8"),sQuery(id+"F2.wireOp",EDGE,"E10")])]}),"instanceName":"69"});
            var Q71;
            Q71=makeQuery(id+"F5.opPattern","COPY",BODY,{"derivedFrom":makeQuery(id+"F3.opExtrude","SWEPT_BODY",BODY,{"disambiguationData":[OSD([sQuery(id+"F2.wireOp",EDGE,"E2"),sQuery(id+"F2.wireOp",EDGE,"E3"),sQuery(id+"F2.wireOp",EDGE,"E4"),sQuery(id+"F2.wireOp",EDGE,"E5.filletArc"),sQuery(id+"F2.wireOp",EDGE,"E6.filletArc"),sQuery(id+"F2.wireOp",EDGE,"E7"),sQuery(id+"F2.wireOp",EDGE,"E8"),sQuery(id+"F2.wireOp",EDGE,"E10")])]}),"instanceName":"70"});
            var Q72;
            Q72=makeQuery(id+"F5.opPattern","COPY",BODY,{"derivedFrom":makeQuery(id+"F3.opExtrude","SWEPT_BODY",BODY,{"disambiguationData":[OSD([sQuery(id+"F2.wireOp",EDGE,"E2"),sQuery(id+"F2.wireOp",EDGE,"E3"),sQuery(id+"F2.wireOp",EDGE,"E4"),sQuery(id+"F2.wireOp",EDGE,"E5.filletArc"),sQuery(id+"F2.wireOp",EDGE,"E6.filletArc"),sQuery(id+"F2.wireOp",EDGE,"E7"),sQuery(id+"F2.wireOp",EDGE,"E8"),sQuery(id+"F2.wireOp",EDGE,"E10")])]}),"instanceName":"71"});
            var Q73;
            Q73=makeQuery(id+"F5.opPattern","COPY",BODY,{"derivedFrom":makeQuery(id+"F3.opExtrude","SWEPT_BODY",BODY,{"disambiguationData":[OSD([sQuery(id+"F2.wireOp",EDGE,"E2"),sQuery(id+"F2.wireOp",EDGE,"E3"),sQuery(id+"F2.wireOp",EDGE,"E4"),sQuery(id+"F2.wireOp",EDGE,"E5.filletArc"),sQuery(id+"F2.wireOp",EDGE,"E6.filletArc"),sQuery(id+"F2.wireOp",EDGE,"E7"),sQuery(id+"F2.wireOp",EDGE,"E8"),sQuery(id+"F2.wireOp",EDGE,"E10")])]}),"instanceName":"72"});
            var Q74;
            Q74=makeQuery(id+"F5.opPattern","COPY",BODY,{"derivedFrom":makeQuery(id+"F3.opExtrude","SWEPT_BODY",BODY,{"disambiguationData":[OSD([sQuery(id+"F2.wireOp",EDGE,"E2"),sQuery(id+"F2.wireOp",EDGE,"E3"),sQuery(id+"F2.wireOp",EDGE,"E4"),sQuery(id+"F2.wireOp",EDGE,"E5.filletArc"),sQuery(id+"F2.wireOp",EDGE,"E6.filletArc"),sQuery(id+"F2.wireOp",EDGE,"E7"),sQuery(id+"F2.wireOp",EDGE,"E8"),sQuery(id+"F2.wireOp",EDGE,"E10")])]}),"instanceName":"73"});
            var Q75;
            Q75=makeQuery(id+"F5.opPattern","COPY",BODY,{"derivedFrom":makeQuery(id+"F3.opExtrude","SWEPT_BODY",BODY,{"disambiguationData":[OSD([sQuery(id+"F2.wireOp",EDGE,"E2"),sQuery(id+"F2.wireOp",EDGE,"E3"),sQuery(id+"F2.wireOp",EDGE,"E4"),sQuery(id+"F2.wireOp",EDGE,"E5.filletArc"),sQuery(id+"F2.wireOp",EDGE,"E6.filletArc"),sQuery(id+"F2.wireOp",EDGE,"E7"),sQuery(id+"F2.wireOp",EDGE,"E8"),sQuery(id+"F2.wireOp",EDGE,"E10")])]}),"instanceName":"74"});
            var Q76;
            Q76=makeQuery(id+"F5.opPattern","COPY",BODY,{"derivedFrom":makeQuery(id+"F3.opExtrude","SWEPT_BODY",BODY,{"disambiguationData":[OSD([sQuery(id+"F2.wireOp",EDGE,"E2"),sQuery(id+"F2.wireOp",EDGE,"E3"),sQuery(id+"F2.wireOp",EDGE,"E4"),sQuery(id+"F2.wireOp",EDGE,"E5.filletArc"),sQuery(id+"F2.wireOp",EDGE,"E6.filletArc"),sQuery(id+"F2.wireOp",EDGE,"E7"),sQuery(id+"F2.wireOp",EDGE,"E8"),sQuery(id+"F2.wireOp",EDGE,"E10")])]}),"instanceName":"75"});
            var Q77;
            Q77=makeQuery(id+"F5.opPattern","COPY",BODY,{"derivedFrom":makeQuery(id+"F3.opExtrude","SWEPT_BODY",BODY,{"disambiguationData":[OSD([sQuery(id+"F2.wireOp",EDGE,"E2"),sQuery(id+"F2.wireOp",EDGE,"E3"),sQuery(id+"F2.wireOp",EDGE,"E4"),sQuery(id+"F2.wireOp",EDGE,"E5.filletArc"),sQuery(id+"F2.wireOp",EDGE,"E6.filletArc"),sQuery(id+"F2.wireOp",EDGE,"E7"),sQuery(id+"F2.wireOp",EDGE,"E8"),sQuery(id+"F2.wireOp",EDGE,"E10")])]}),"instanceName":"76"});
            var Q78;
            Q78=makeQuery(id+"F5.opPattern","COPY",BODY,{"derivedFrom":makeQuery(id+"F3.opExtrude","SWEPT_BODY",BODY,{"disambiguationData":[OSD([sQuery(id+"F2.wireOp",EDGE,"E2"),sQuery(id+"F2.wireOp",EDGE,"E3"),sQuery(id+"F2.wireOp",EDGE,"E4"),sQuery(id+"F2.wireOp",EDGE,"E5.filletArc"),sQuery(id+"F2.wireOp",EDGE,"E6.filletArc"),sQuery(id+"F2.wireOp",EDGE,"E7"),sQuery(id+"F2.wireOp",EDGE,"E8"),sQuery(id+"F2.wireOp",EDGE,"E10")])]}),"instanceName":"77"});
            var Q79;
            Q79=makeQuery(id+"F5.opPattern","COPY",BODY,{"derivedFrom":makeQuery(id+"F3.opExtrude","SWEPT_BODY",BODY,{"disambiguationData":[OSD([sQuery(id+"F2.wireOp",EDGE,"E2"),sQuery(id+"F2.wireOp",EDGE,"E3"),sQuery(id+"F2.wireOp",EDGE,"E4"),sQuery(id+"F2.wireOp",EDGE,"E5.filletArc"),sQuery(id+"F2.wireOp",EDGE,"E6.filletArc"),sQuery(id+"F2.wireOp",EDGE,"E7"),sQuery(id+"F2.wireOp",EDGE,"E8"),sQuery(id+"F2.wireOp",EDGE,"E10")])]}),"instanceName":"78"});
            var Q80;
            Q80=makeQuery(id+"F5.opPattern","COPY",BODY,{"derivedFrom":makeQuery(id+"F3.opExtrude","SWEPT_BODY",BODY,{"disambiguationData":[OSD([sQuery(id+"F2.wireOp",EDGE,"E2"),sQuery(id+"F2.wireOp",EDGE,"E3"),sQuery(id+"F2.wireOp",EDGE,"E4"),sQuery(id+"F2.wireOp",EDGE,"E5.filletArc"),sQuery(id+"F2.wireOp",EDGE,"E6.filletArc"),sQuery(id+"F2.wireOp",EDGE,"E7"),sQuery(id+"F2.wireOp",EDGE,"E8"),sQuery(id+"F2.wireOp",EDGE,"E10")])]}),"instanceName":"79"});
            var Q81;
            Q81=makeQuery(id+"F5.opPattern","COPY",BODY,{"derivedFrom":makeQuery(id+"F3.opExtrude","SWEPT_BODY",BODY,{"disambiguationData":[OSD([sQuery(id+"F2.wireOp",EDGE,"E2"),sQuery(id+"F2.wireOp",EDGE,"E3"),sQuery(id+"F2.wireOp",EDGE,"E4"),sQuery(id+"F2.wireOp",EDGE,"E5.filletArc"),sQuery(id+"F2.wireOp",EDGE,"E6.filletArc"),sQuery(id+"F2.wireOp",EDGE,"E7"),sQuery(id+"F2.wireOp",EDGE,"E8"),sQuery(id+"F2.wireOp",EDGE,"E10")])]}),"instanceName":"80"});
            var Q82;
            Q82=makeQuery(id+"F5.opPattern","COPY",BODY,{"derivedFrom":makeQuery(id+"F3.opExtrude","SWEPT_BODY",BODY,{"disambiguationData":[OSD([sQuery(id+"F2.wireOp",EDGE,"E2"),sQuery(id+"F2.wireOp",EDGE,"E3"),sQuery(id+"F2.wireOp",EDGE,"E4"),sQuery(id+"F2.wireOp",EDGE,"E5.filletArc"),sQuery(id+"F2.wireOp",EDGE,"E6.filletArc"),sQuery(id+"F2.wireOp",EDGE,"E7"),sQuery(id+"F2.wireOp",EDGE,"E8"),sQuery(id+"F2.wireOp",EDGE,"E10")])]}),"instanceName":"81"});
            var Q83;
            Q83=makeQuery(id+"F5.opPattern","COPY",BODY,{"derivedFrom":makeQuery(id+"F3.opExtrude","SWEPT_BODY",BODY,{"disambiguationData":[OSD([sQuery(id+"F2.wireOp",EDGE,"E2"),sQuery(id+"F2.wireOp",EDGE,"E3"),sQuery(id+"F2.wireOp",EDGE,"E4"),sQuery(id+"F2.wireOp",EDGE,"E5.filletArc"),sQuery(id+"F2.wireOp",EDGE,"E6.filletArc"),sQuery(id+"F2.wireOp",EDGE,"E7"),sQuery(id+"F2.wireOp",EDGE,"E8"),sQuery(id+"F2.wireOp",EDGE,"E10")])]}),"instanceName":"82"});
            var Q84;
            Q84=makeQuery(id+"F5.opPattern","COPY",BODY,{"derivedFrom":makeQuery(id+"F3.opExtrude","SWEPT_BODY",BODY,{"disambiguationData":[OSD([sQuery(id+"F2.wireOp",EDGE,"E2"),sQuery(id+"F2.wireOp",EDGE,"E3"),sQuery(id+"F2.wireOp",EDGE,"E4"),sQuery(id+"F2.wireOp",EDGE,"E5.filletArc"),sQuery(id+"F2.wireOp",EDGE,"E6.filletArc"),sQuery(id+"F2.wireOp",EDGE,"E7"),sQuery(id+"F2.wireOp",EDGE,"E8"),sQuery(id+"F2.wireOp",EDGE,"E10")])]}),"instanceName":"83"});
            var Q85;
            Q85=makeQuery(id+"F5.opPattern","COPY",BODY,{"derivedFrom":makeQuery(id+"F3.opExtrude","SWEPT_BODY",BODY,{"disambiguationData":[OSD([sQuery(id+"F2.wireOp",EDGE,"E2"),sQuery(id+"F2.wireOp",EDGE,"E3"),sQuery(id+"F2.wireOp",EDGE,"E4"),sQuery(id+"F2.wireOp",EDGE,"E5.filletArc"),sQuery(id+"F2.wireOp",EDGE,"E6.filletArc"),sQuery(id+"F2.wireOp",EDGE,"E7"),sQuery(id+"F2.wireOp",EDGE,"E8"),sQuery(id+"F2.wireOp",EDGE,"E10")])]}),"instanceName":"84"});
            var Q86;
            Q86=makeQuery(id+"F5.opPattern","COPY",BODY,{"derivedFrom":makeQuery(id+"F3.opExtrude","SWEPT_BODY",BODY,{"disambiguationData":[OSD([sQuery(id+"F2.wireOp",EDGE,"E2"),sQuery(id+"F2.wireOp",EDGE,"E3"),sQuery(id+"F2.wireOp",EDGE,"E4"),sQuery(id+"F2.wireOp",EDGE,"E5.filletArc"),sQuery(id+"F2.wireOp",EDGE,"E6.filletArc"),sQuery(id+"F2.wireOp",EDGE,"E7"),sQuery(id+"F2.wireOp",EDGE,"E8"),sQuery(id+"F2.wireOp",EDGE,"E10")])]}),"instanceName":"85"});
            var Q87;
            Q87=makeQuery(id+"F5.opPattern","COPY",BODY,{"derivedFrom":makeQuery(id+"F3.opExtrude","SWEPT_BODY",BODY,{"disambiguationData":[OSD([sQuery(id+"F2.wireOp",EDGE,"E2"),sQuery(id+"F2.wireOp",EDGE,"E3"),sQuery(id+"F2.wireOp",EDGE,"E4"),sQuery(id+"F2.wireOp",EDGE,"E5.filletArc"),sQuery(id+"F2.wireOp",EDGE,"E6.filletArc"),sQuery(id+"F2.wireOp",EDGE,"E7"),sQuery(id+"F2.wireOp",EDGE,"E8"),sQuery(id+"F2.wireOp",EDGE,"E10")])]}),"instanceName":"86"});
            var Q88;
            Q88=makeQuery(id+"F5.opPattern","COPY",BODY,{"derivedFrom":makeQuery(id+"F3.opExtrude","SWEPT_BODY",BODY,{"disambiguationData":[OSD([sQuery(id+"F2.wireOp",EDGE,"E2"),sQuery(id+"F2.wireOp",EDGE,"E3"),sQuery(id+"F2.wireOp",EDGE,"E4"),sQuery(id+"F2.wireOp",EDGE,"E5.filletArc"),sQuery(id+"F2.wireOp",EDGE,"E6.filletArc"),sQuery(id+"F2.wireOp",EDGE,"E7"),sQuery(id+"F2.wireOp",EDGE,"E8"),sQuery(id+"F2.wireOp",EDGE,"E10")])]}),"instanceName":"87"});
            var Q89;
            Q89=makeQuery(id+"F5.opPattern","COPY",BODY,{"derivedFrom":makeQuery(id+"F3.opExtrude","SWEPT_BODY",BODY,{"disambiguationData":[OSD([sQuery(id+"F2.wireOp",EDGE,"E2"),sQuery(id+"F2.wireOp",EDGE,"E3"),sQuery(id+"F2.wireOp",EDGE,"E4"),sQuery(id+"F2.wireOp",EDGE,"E5.filletArc"),sQuery(id+"F2.wireOp",EDGE,"E6.filletArc"),sQuery(id+"F2.wireOp",EDGE,"E7"),sQuery(id+"F2.wireOp",EDGE,"E8"),sQuery(id+"F2.wireOp",EDGE,"E10")])]}),"instanceName":"88"});
            var Q90;
            Q90=makeQuery(id+"F5.opPattern","COPY",BODY,{"derivedFrom":makeQuery(id+"F3.opExtrude","SWEPT_BODY",BODY,{"disambiguationData":[OSD([sQuery(id+"F2.wireOp",EDGE,"E2"),sQuery(id+"F2.wireOp",EDGE,"E3"),sQuery(id+"F2.wireOp",EDGE,"E4"),sQuery(id+"F2.wireOp",EDGE,"E5.filletArc"),sQuery(id+"F2.wireOp",EDGE,"E6.filletArc"),sQuery(id+"F2.wireOp",EDGE,"E7"),sQuery(id+"F2.wireOp",EDGE,"E8"),sQuery(id+"F2.wireOp",EDGE,"E10")])]}),"instanceName":"89"});
            var Q91;
            Q91=makeQuery(id+"F5.opPattern","COPY",BODY,{"derivedFrom":makeQuery(id+"F3.opExtrude","SWEPT_BODY",BODY,{"disambiguationData":[OSD([sQuery(id+"F2.wireOp",EDGE,"E2"),sQuery(id+"F2.wireOp",EDGE,"E3"),sQuery(id+"F2.wireOp",EDGE,"E4"),sQuery(id+"F2.wireOp",EDGE,"E5.filletArc"),sQuery(id+"F2.wireOp",EDGE,"E6.filletArc"),sQuery(id+"F2.wireOp",EDGE,"E7"),sQuery(id+"F2.wireOp",EDGE,"E8"),sQuery(id+"F2.wireOp",EDGE,"E10")])]}),"instanceName":"90"});
            var Q92;
            Q92=makeQuery(id+"F5.opPattern","COPY",BODY,{"derivedFrom":makeQuery(id+"F3.opExtrude","SWEPT_BODY",BODY,{"disambiguationData":[OSD([sQuery(id+"F2.wireOp",EDGE,"E2"),sQuery(id+"F2.wireOp",EDGE,"E3"),sQuery(id+"F2.wireOp",EDGE,"E4"),sQuery(id+"F2.wireOp",EDGE,"E5.filletArc"),sQuery(id+"F2.wireOp",EDGE,"E6.filletArc"),sQuery(id+"F2.wireOp",EDGE,"E7"),sQuery(id+"F2.wireOp",EDGE,"E8"),sQuery(id+"F2.wireOp",EDGE,"E10")])]}),"instanceName":"91"});
            var Q93;
            Q93=makeQuery(id+"F5.opPattern","COPY",BODY,{"derivedFrom":makeQuery(id+"F3.opExtrude","SWEPT_BODY",BODY,{"disambiguationData":[OSD([sQuery(id+"F2.wireOp",EDGE,"E2"),sQuery(id+"F2.wireOp",EDGE,"E3"),sQuery(id+"F2.wireOp",EDGE,"E4"),sQuery(id+"F2.wireOp",EDGE,"E5.filletArc"),sQuery(id+"F2.wireOp",EDGE,"E6.filletArc"),sQuery(id+"F2.wireOp",EDGE,"E7"),sQuery(id+"F2.wireOp",EDGE,"E8"),sQuery(id+"F2.wireOp",EDGE,"E10")])]}),"instanceName":"92"});
            var Q94;
            Q94=makeQuery(id+"F5.opPattern","COPY",BODY,{"derivedFrom":makeQuery(id+"F3.opExtrude","SWEPT_BODY",BODY,{"disambiguationData":[OSD([sQuery(id+"F2.wireOp",EDGE,"E2"),sQuery(id+"F2.wireOp",EDGE,"E3"),sQuery(id+"F2.wireOp",EDGE,"E4"),sQuery(id+"F2.wireOp",EDGE,"E5.filletArc"),sQuery(id+"F2.wireOp",EDGE,"E6.filletArc"),sQuery(id+"F2.wireOp",EDGE,"E7"),sQuery(id+"F2.wireOp",EDGE,"E8"),sQuery(id+"F2.wireOp",EDGE,"E10")])]}),"instanceName":"93"});
            var Q95;
            Q95=makeQuery(id+"F5.opPattern","COPY",BODY,{"derivedFrom":makeQuery(id+"F3.opExtrude","SWEPT_BODY",BODY,{"disambiguationData":[OSD([sQuery(id+"F2.wireOp",EDGE,"E2"),sQuery(id+"F2.wireOp",EDGE,"E3"),sQuery(id+"F2.wireOp",EDGE,"E4"),sQuery(id+"F2.wireOp",EDGE,"E5.filletArc"),sQuery(id+"F2.wireOp",EDGE,"E6.filletArc"),sQuery(id+"F2.wireOp",EDGE,"E7"),sQuery(id+"F2.wireOp",EDGE,"E8"),sQuery(id+"F2.wireOp",EDGE,"E10")])]}),"instanceName":"94"});
            var Q96;
            Q96=makeQuery(id+"F5.opPattern","COPY",BODY,{"derivedFrom":makeQuery(id+"F3.opExtrude","SWEPT_BODY",BODY,{"disambiguationData":[OSD([sQuery(id+"F2.wireOp",EDGE,"E2"),sQuery(id+"F2.wireOp",EDGE,"E3"),sQuery(id+"F2.wireOp",EDGE,"E4"),sQuery(id+"F2.wireOp",EDGE,"E5.filletArc"),sQuery(id+"F2.wireOp",EDGE,"E6.filletArc"),sQuery(id+"F2.wireOp",EDGE,"E7"),sQuery(id+"F2.wireOp",EDGE,"E8"),sQuery(id+"F2.wireOp",EDGE,"E10")])]}),"instanceName":"95"});
            var Q97;
            Q97=makeQuery(id+"F5.opPattern","COPY",BODY,{"derivedFrom":makeQuery(id+"F3.opExtrude","SWEPT_BODY",BODY,{"disambiguationData":[OSD([sQuery(id+"F2.wireOp",EDGE,"E2"),sQuery(id+"F2.wireOp",EDGE,"E3"),sQuery(id+"F2.wireOp",EDGE,"E4"),sQuery(id+"F2.wireOp",EDGE,"E5.filletArc"),sQuery(id+"F2.wireOp",EDGE,"E6.filletArc"),sQuery(id+"F2.wireOp",EDGE,"E7"),sQuery(id+"F2.wireOp",EDGE,"E8"),sQuery(id+"F2.wireOp",EDGE,"E10")])]}),"instanceName":"96"});
            var Q98;
            Q98=makeQuery(id+"F5.opPattern","COPY",BODY,{"derivedFrom":makeQuery(id+"F3.opExtrude","SWEPT_BODY",BODY,{"disambiguationData":[OSD([sQuery(id+"F2.wireOp",EDGE,"E2"),sQuery(id+"F2.wireOp",EDGE,"E3"),sQuery(id+"F2.wireOp",EDGE,"E4"),sQuery(id+"F2.wireOp",EDGE,"E5.filletArc"),sQuery(id+"F2.wireOp",EDGE,"E6.filletArc"),sQuery(id+"F2.wireOp",EDGE,"E7"),sQuery(id+"F2.wireOp",EDGE,"E8"),sQuery(id+"F2.wireOp",EDGE,"E10")])]}),"instanceName":"97"});
            var Q99;
            Q99=makeQuery(id+"F5.opPattern","COPY",BODY,{"derivedFrom":makeQuery(id+"F3.opExtrude","SWEPT_BODY",BODY,{"disambiguationData":[OSD([sQuery(id+"F2.wireOp",EDGE,"E2"),sQuery(id+"F2.wireOp",EDGE,"E3"),sQuery(id+"F2.wireOp",EDGE,"E4"),sQuery(id+"F2.wireOp",EDGE,"E5.filletArc"),sQuery(id+"F2.wireOp",EDGE,"E6.filletArc"),sQuery(id+"F2.wireOp",EDGE,"E7"),sQuery(id+"F2.wireOp",EDGE,"E8"),sQuery(id+"F2.wireOp",EDGE,"E10")])]}),"instanceName":"98"});
            var Q100;
            Q100=makeQuery(id+"F5.opPattern","COPY",BODY,{"derivedFrom":makeQuery(id+"F3.opExtrude","SWEPT_BODY",BODY,{"disambiguationData":[OSD([sQuery(id+"F2.wireOp",EDGE,"E2"),sQuery(id+"F2.wireOp",EDGE,"E3"),sQuery(id+"F2.wireOp",EDGE,"E4"),sQuery(id+"F2.wireOp",EDGE,"E5.filletArc"),sQuery(id+"F2.wireOp",EDGE,"E6.filletArc"),sQuery(id+"F2.wireOp",EDGE,"E7"),sQuery(id+"F2.wireOp",EDGE,"E8"),sQuery(id+"F2.wireOp",EDGE,"E10")])]}),"instanceName":"99"});
            var Q101;
            Q101=makeQuery(id+"F5.opPattern","COPY",BODY,{"derivedFrom":makeQuery(id+"F3.opExtrude","SWEPT_BODY",BODY,{"disambiguationData":[OSD([sQuery(id+"F2.wireOp",EDGE,"E2"),sQuery(id+"F2.wireOp",EDGE,"E3"),sQuery(id+"F2.wireOp",EDGE,"E4"),sQuery(id+"F2.wireOp",EDGE,"E5.filletArc"),sQuery(id+"F2.wireOp",EDGE,"E6.filletArc"),sQuery(id+"F2.wireOp",EDGE,"E7"),sQuery(id+"F2.wireOp",EDGE,"E8"),sQuery(id+"F2.wireOp",EDGE,"E10")])]}),"instanceName":"100"});
            var Q102;
            Q102=makeQuery(id+"F5.opPattern","COPY",BODY,{"derivedFrom":makeQuery(id+"F3.opExtrude","SWEPT_BODY",BODY,{"disambiguationData":[OSD([sQuery(id+"F2.wireOp",EDGE,"E2"),sQuery(id+"F2.wireOp",EDGE,"E3"),sQuery(id+"F2.wireOp",EDGE,"E4"),sQuery(id+"F2.wireOp",EDGE,"E5.filletArc"),sQuery(id+"F2.wireOp",EDGE,"E6.filletArc"),sQuery(id+"F2.wireOp",EDGE,"E7"),sQuery(id+"F2.wireOp",EDGE,"E8"),sQuery(id+"F2.wireOp",EDGE,"E10")])]}),"instanceName":"101"});
            var Q103;
            Q103=makeQuery(id+"F5.opPattern","COPY",BODY,{"derivedFrom":makeQuery(id+"F3.opExtrude","SWEPT_BODY",BODY,{"disambiguationData":[OSD([sQuery(id+"F2.wireOp",EDGE,"E2"),sQuery(id+"F2.wireOp",EDGE,"E3"),sQuery(id+"F2.wireOp",EDGE,"E4"),sQuery(id+"F2.wireOp",EDGE,"E5.filletArc"),sQuery(id+"F2.wireOp",EDGE,"E6.filletArc"),sQuery(id+"F2.wireOp",EDGE,"E7"),sQuery(id+"F2.wireOp",EDGE,"E8"),sQuery(id+"F2.wireOp",EDGE,"E10")])]}),"instanceName":"102"});
            var Q104;
            Q104=makeQuery(id+"F5.opPattern","COPY",BODY,{"derivedFrom":makeQuery(id+"F3.opExtrude","SWEPT_BODY",BODY,{"disambiguationData":[OSD([sQuery(id+"F2.wireOp",EDGE,"E2"),sQuery(id+"F2.wireOp",EDGE,"E3"),sQuery(id+"F2.wireOp",EDGE,"E4"),sQuery(id+"F2.wireOp",EDGE,"E5.filletArc"),sQuery(id+"F2.wireOp",EDGE,"E6.filletArc"),sQuery(id+"F2.wireOp",EDGE,"E7"),sQuery(id+"F2.wireOp",EDGE,"E8"),sQuery(id+"F2.wireOp",EDGE,"E10")])]}),"instanceName":"103"});
            var Q105;
            Q105=makeQuery(id+"F5.opPattern","COPY",BODY,{"derivedFrom":makeQuery(id+"F3.opExtrude","SWEPT_BODY",BODY,{"disambiguationData":[OSD([sQuery(id+"F2.wireOp",EDGE,"E2"),sQuery(id+"F2.wireOp",EDGE,"E3"),sQuery(id+"F2.wireOp",EDGE,"E4"),sQuery(id+"F2.wireOp",EDGE,"E5.filletArc"),sQuery(id+"F2.wireOp",EDGE,"E6.filletArc"),sQuery(id+"F2.wireOp",EDGE,"E7"),sQuery(id+"F2.wireOp",EDGE,"E8"),sQuery(id+"F2.wireOp",EDGE,"E10")])]}),"instanceName":"104"});
            var Q106;
            Q106=makeQuery(id+"F5.opPattern","COPY",BODY,{"derivedFrom":makeQuery(id+"F3.opExtrude","SWEPT_BODY",BODY,{"disambiguationData":[OSD([sQuery(id+"F2.wireOp",EDGE,"E2"),sQuery(id+"F2.wireOp",EDGE,"E3"),sQuery(id+"F2.wireOp",EDGE,"E4"),sQuery(id+"F2.wireOp",EDGE,"E5.filletArc"),sQuery(id+"F2.wireOp",EDGE,"E6.filletArc"),sQuery(id+"F2.wireOp",EDGE,"E7"),sQuery(id+"F2.wireOp",EDGE,"E8"),sQuery(id+"F2.wireOp",EDGE,"E10")])]}),"instanceName":"105"});
            var Q107;
            Q107=makeQuery(id+"F5.opPattern","COPY",BODY,{"derivedFrom":makeQuery(id+"F3.opExtrude","SWEPT_BODY",BODY,{"disambiguationData":[OSD([sQuery(id+"F2.wireOp",EDGE,"E2"),sQuery(id+"F2.wireOp",EDGE,"E3"),sQuery(id+"F2.wireOp",EDGE,"E4"),sQuery(id+"F2.wireOp",EDGE,"E5.filletArc"),sQuery(id+"F2.wireOp",EDGE,"E6.filletArc"),sQuery(id+"F2.wireOp",EDGE,"E7"),sQuery(id+"F2.wireOp",EDGE,"E8"),sQuery(id+"F2.wireOp",EDGE,"E10")])]}),"instanceName":"106"});
            var Q108;
            Q108=makeQuery(id+"F5.opPattern","COPY",BODY,{"derivedFrom":makeQuery(id+"F3.opExtrude","SWEPT_BODY",BODY,{"disambiguationData":[OSD([sQuery(id+"F2.wireOp",EDGE,"E2"),sQuery(id+"F2.wireOp",EDGE,"E3"),sQuery(id+"F2.wireOp",EDGE,"E4"),sQuery(id+"F2.wireOp",EDGE,"E5.filletArc"),sQuery(id+"F2.wireOp",EDGE,"E6.filletArc"),sQuery(id+"F2.wireOp",EDGE,"E7"),sQuery(id+"F2.wireOp",EDGE,"E8"),sQuery(id+"F2.wireOp",EDGE,"E10")])]}),"instanceName":"107"});
            var Q109;
            Q109=makeQuery(id+"F5.opPattern","COPY",BODY,{"derivedFrom":makeQuery(id+"F3.opExtrude","SWEPT_BODY",BODY,{"disambiguationData":[OSD([sQuery(id+"F2.wireOp",EDGE,"E2"),sQuery(id+"F2.wireOp",EDGE,"E3"),sQuery(id+"F2.wireOp",EDGE,"E4"),sQuery(id+"F2.wireOp",EDGE,"E5.filletArc"),sQuery(id+"F2.wireOp",EDGE,"E6.filletArc"),sQuery(id+"F2.wireOp",EDGE,"E7"),sQuery(id+"F2.wireOp",EDGE,"E8"),sQuery(id+"F2.wireOp",EDGE,"E10")])]}),"instanceName":"108"});
            var Q110;
            Q110=makeQuery(id+"F5.opPattern","COPY",BODY,{"derivedFrom":makeQuery(id+"F3.opExtrude","SWEPT_BODY",BODY,{"disambiguationData":[OSD([sQuery(id+"F2.wireOp",EDGE,"E2"),sQuery(id+"F2.wireOp",EDGE,"E3"),sQuery(id+"F2.wireOp",EDGE,"E4"),sQuery(id+"F2.wireOp",EDGE,"E5.filletArc"),sQuery(id+"F2.wireOp",EDGE,"E6.filletArc"),sQuery(id+"F2.wireOp",EDGE,"E7"),sQuery(id+"F2.wireOp",EDGE,"E8"),sQuery(id+"F2.wireOp",EDGE,"E10")])]}),"instanceName":"109"});
            var Q111;
            Q111=makeQuery(id+"F5.opPattern","COPY",BODY,{"derivedFrom":makeQuery(id+"F3.opExtrude","SWEPT_BODY",BODY,{"disambiguationData":[OSD([sQuery(id+"F2.wireOp",EDGE,"E2"),sQuery(id+"F2.wireOp",EDGE,"E3"),sQuery(id+"F2.wireOp",EDGE,"E4"),sQuery(id+"F2.wireOp",EDGE,"E5.filletArc"),sQuery(id+"F2.wireOp",EDGE,"E6.filletArc"),sQuery(id+"F2.wireOp",EDGE,"E7"),sQuery(id+"F2.wireOp",EDGE,"E8"),sQuery(id+"F2.wireOp",EDGE,"E10")])]}),"instanceName":"110"});
            var Q112;
            Q112=makeQuery(id+"F5.opPattern","COPY",BODY,{"derivedFrom":makeQuery(id+"F3.opExtrude","SWEPT_BODY",BODY,{"disambiguationData":[OSD([sQuery(id+"F2.wireOp",EDGE,"E2"),sQuery(id+"F2.wireOp",EDGE,"E3"),sQuery(id+"F2.wireOp",EDGE,"E4"),sQuery(id+"F2.wireOp",EDGE,"E5.filletArc"),sQuery(id+"F2.wireOp",EDGE,"E6.filletArc"),sQuery(id+"F2.wireOp",EDGE,"E7"),sQuery(id+"F2.wireOp",EDGE,"E8"),sQuery(id+"F2.wireOp",EDGE,"E10")])]}),"instanceName":"111"});
            var Q113;
            Q113=makeQuery(id+"F5.opPattern","COPY",BODY,{"derivedFrom":makeQuery(id+"F3.opExtrude","SWEPT_BODY",BODY,{"disambiguationData":[OSD([sQuery(id+"F2.wireOp",EDGE,"E2"),sQuery(id+"F2.wireOp",EDGE,"E3"),sQuery(id+"F2.wireOp",EDGE,"E4"),sQuery(id+"F2.wireOp",EDGE,"E5.filletArc"),sQuery(id+"F2.wireOp",EDGE,"E6.filletArc"),sQuery(id+"F2.wireOp",EDGE,"E7"),sQuery(id+"F2.wireOp",EDGE,"E8"),sQuery(id+"F2.wireOp",EDGE,"E10")])]}),"instanceName":"112"});
            var Q114;
            Q114=makeQuery(id+"F5.opPattern","COPY",BODY,{"derivedFrom":makeQuery(id+"F3.opExtrude","SWEPT_BODY",BODY,{"disambiguationData":[OSD([sQuery(id+"F2.wireOp",EDGE,"E2"),sQuery(id+"F2.wireOp",EDGE,"E3"),sQuery(id+"F2.wireOp",EDGE,"E4"),sQuery(id+"F2.wireOp",EDGE,"E5.filletArc"),sQuery(id+"F2.wireOp",EDGE,"E6.filletArc"),sQuery(id+"F2.wireOp",EDGE,"E7"),sQuery(id+"F2.wireOp",EDGE,"E8"),sQuery(id+"F2.wireOp",EDGE,"E10")])]}),"instanceName":"113"});
            var Q115;
            Q115=makeQuery(id+"F5.opPattern","COPY",BODY,{"derivedFrom":makeQuery(id+"F3.opExtrude","SWEPT_BODY",BODY,{"disambiguationData":[OSD([sQuery(id+"F2.wireOp",EDGE,"E2"),sQuery(id+"F2.wireOp",EDGE,"E3"),sQuery(id+"F2.wireOp",EDGE,"E4"),sQuery(id+"F2.wireOp",EDGE,"E5.filletArc"),sQuery(id+"F2.wireOp",EDGE,"E6.filletArc"),sQuery(id+"F2.wireOp",EDGE,"E7"),sQuery(id+"F2.wireOp",EDGE,"E8"),sQuery(id+"F2.wireOp",EDGE,"E10")])]}),"instanceName":"114"});
            var Q116;
            Q116=makeQuery(id+"F5.opPattern","COPY",BODY,{"derivedFrom":makeQuery(id+"F3.opExtrude","SWEPT_BODY",BODY,{"disambiguationData":[OSD([sQuery(id+"F2.wireOp",EDGE,"E2"),sQuery(id+"F2.wireOp",EDGE,"E3"),sQuery(id+"F2.wireOp",EDGE,"E4"),sQuery(id+"F2.wireOp",EDGE,"E5.filletArc"),sQuery(id+"F2.wireOp",EDGE,"E6.filletArc"),sQuery(id+"F2.wireOp",EDGE,"E7"),sQuery(id+"F2.wireOp",EDGE,"E8"),sQuery(id+"F2.wireOp",EDGE,"E10")])]}),"instanceName":"115"});
            var Q117;
            Q117=makeQuery(id+"F5.opPattern","COPY",BODY,{"derivedFrom":makeQuery(id+"F3.opExtrude","SWEPT_BODY",BODY,{"disambiguationData":[OSD([sQuery(id+"F2.wireOp",EDGE,"E2"),sQuery(id+"F2.wireOp",EDGE,"E3"),sQuery(id+"F2.wireOp",EDGE,"E4"),sQuery(id+"F2.wireOp",EDGE,"E5.filletArc"),sQuery(id+"F2.wireOp",EDGE,"E6.filletArc"),sQuery(id+"F2.wireOp",EDGE,"E7"),sQuery(id+"F2.wireOp",EDGE,"E8"),sQuery(id+"F2.wireOp",EDGE,"E10")])]}),"instanceName":"116"});
            var Q118;
            Q118=makeQuery(id+"F5.opPattern","COPY",BODY,{"derivedFrom":makeQuery(id+"F3.opExtrude","SWEPT_BODY",BODY,{"disambiguationData":[OSD([sQuery(id+"F2.wireOp",EDGE,"E2"),sQuery(id+"F2.wireOp",EDGE,"E3"),sQuery(id+"F2.wireOp",EDGE,"E4"),sQuery(id+"F2.wireOp",EDGE,"E5.filletArc"),sQuery(id+"F2.wireOp",EDGE,"E6.filletArc"),sQuery(id+"F2.wireOp",EDGE,"E7"),sQuery(id+"F2.wireOp",EDGE,"E8"),sQuery(id+"F2.wireOp",EDGE,"E10")])]}),"instanceName":"117"});
            var Q119;
            Q119=makeQuery(id+"F5.opPattern","COPY",BODY,{"derivedFrom":makeQuery(id+"F3.opExtrude","SWEPT_BODY",BODY,{"disambiguationData":[OSD([sQuery(id+"F2.wireOp",EDGE,"E2"),sQuery(id+"F2.wireOp",EDGE,"E3"),sQuery(id+"F2.wireOp",EDGE,"E4"),sQuery(id+"F2.wireOp",EDGE,"E5.filletArc"),sQuery(id+"F2.wireOp",EDGE,"E6.filletArc"),sQuery(id+"F2.wireOp",EDGE,"E7"),sQuery(id+"F2.wireOp",EDGE,"E8"),sQuery(id+"F2.wireOp",EDGE,"E10")])]}),"instanceName":"118"});
            var Q120;
            Q120=makeQuery(id+"F5.opPattern","COPY",BODY,{"derivedFrom":makeQuery(id+"F3.opExtrude","SWEPT_BODY",BODY,{"disambiguationData":[OSD([sQuery(id+"F2.wireOp",EDGE,"E2"),sQuery(id+"F2.wireOp",EDGE,"E3"),sQuery(id+"F2.wireOp",EDGE,"E4"),sQuery(id+"F2.wireOp",EDGE,"E5.filletArc"),sQuery(id+"F2.wireOp",EDGE,"E6.filletArc"),sQuery(id+"F2.wireOp",EDGE,"E7"),sQuery(id+"F2.wireOp",EDGE,"E8"),sQuery(id+"F2.wireOp",EDGE,"E10")])]}),"instanceName":"119"});
            var Q121;
            Q121=makeQuery(id+"F5.opPattern","COPY",BODY,{"derivedFrom":makeQuery(id+"F3.opExtrude","SWEPT_BODY",BODY,{"disambiguationData":[OSD([sQuery(id+"F2.wireOp",EDGE,"E2"),sQuery(id+"F2.wireOp",EDGE,"E3"),sQuery(id+"F2.wireOp",EDGE,"E4"),sQuery(id+"F2.wireOp",EDGE,"E5.filletArc"),sQuery(id+"F2.wireOp",EDGE,"E6.filletArc"),sQuery(id+"F2.wireOp",EDGE,"E7"),sQuery(id+"F2.wireOp",EDGE,"E8"),sQuery(id+"F2.wireOp",EDGE,"E10")])]}),"instanceName":"120"});
            var Q122;
            Q122=makeQuery(id+"F5.opPattern","COPY",BODY,{"derivedFrom":makeQuery(id+"F3.opExtrude","SWEPT_BODY",BODY,{"disambiguationData":[OSD([sQuery(id+"F2.wireOp",EDGE,"E2"),sQuery(id+"F2.wireOp",EDGE,"E3"),sQuery(id+"F2.wireOp",EDGE,"E4"),sQuery(id+"F2.wireOp",EDGE,"E5.filletArc"),sQuery(id+"F2.wireOp",EDGE,"E6.filletArc"),sQuery(id+"F2.wireOp",EDGE,"E7"),sQuery(id+"F2.wireOp",EDGE,"E8"),sQuery(id+"F2.wireOp",EDGE,"E10")])]}),"instanceName":"121"});
            var Q123;
            Q123=makeQuery(id+"F5.opPattern","COPY",BODY,{"derivedFrom":makeQuery(id+"F3.opExtrude","SWEPT_BODY",BODY,{"disambiguationData":[OSD([sQuery(id+"F2.wireOp",EDGE,"E2"),sQuery(id+"F2.wireOp",EDGE,"E3"),sQuery(id+"F2.wireOp",EDGE,"E4"),sQuery(id+"F2.wireOp",EDGE,"E5.filletArc"),sQuery(id+"F2.wireOp",EDGE,"E6.filletArc"),sQuery(id+"F2.wireOp",EDGE,"E7"),sQuery(id+"F2.wireOp",EDGE,"E8"),sQuery(id+"F2.wireOp",EDGE,"E10")])]}),"instanceName":"122"});
            var Q124;
            Q124=makeQuery(id+"F5.opPattern","COPY",BODY,{"derivedFrom":makeQuery(id+"F3.opExtrude","SWEPT_BODY",BODY,{"disambiguationData":[OSD([sQuery(id+"F2.wireOp",EDGE,"E2"),sQuery(id+"F2.wireOp",EDGE,"E3"),sQuery(id+"F2.wireOp",EDGE,"E4"),sQuery(id+"F2.wireOp",EDGE,"E5.filletArc"),sQuery(id+"F2.wireOp",EDGE,"E6.filletArc"),sQuery(id+"F2.wireOp",EDGE,"E7"),sQuery(id+"F2.wireOp",EDGE,"E8"),sQuery(id+"F2.wireOp",EDGE,"E10")])]}),"instanceName":"123"});
            var Q125;
            Q125=makeQuery(id+"F5.opPattern","COPY",BODY,{"derivedFrom":makeQuery(id+"F3.opExtrude","SWEPT_BODY",BODY,{"disambiguationData":[OSD([sQuery(id+"F2.wireOp",EDGE,"E2"),sQuery(id+"F2.wireOp",EDGE,"E3"),sQuery(id+"F2.wireOp",EDGE,"E4"),sQuery(id+"F2.wireOp",EDGE,"E5.filletArc"),sQuery(id+"F2.wireOp",EDGE,"E6.filletArc"),sQuery(id+"F2.wireOp",EDGE,"E7"),sQuery(id+"F2.wireOp",EDGE,"E8"),sQuery(id+"F2.wireOp",EDGE,"E10")])]}),"instanceName":"124"});
            var Q126;
            Q126=makeQuery(id+"F5.opPattern","COPY",BODY,{"derivedFrom":makeQuery(id+"F3.opExtrude","SWEPT_BODY",BODY,{"disambiguationData":[OSD([sQuery(id+"F2.wireOp",EDGE,"E2"),sQuery(id+"F2.wireOp",EDGE,"E3"),sQuery(id+"F2.wireOp",EDGE,"E4"),sQuery(id+"F2.wireOp",EDGE,"E5.filletArc"),sQuery(id+"F2.wireOp",EDGE,"E6.filletArc"),sQuery(id+"F2.wireOp",EDGE,"E7"),sQuery(id+"F2.wireOp",EDGE,"E8"),sQuery(id+"F2.wireOp",EDGE,"E10")])]}),"instanceName":"125"});
            var Q127;
            Q127=makeQuery(id+"F5.opPattern","COPY",BODY,{"derivedFrom":makeQuery(id+"F3.opExtrude","SWEPT_BODY",BODY,{"disambiguationData":[OSD([sQuery(id+"F2.wireOp",EDGE,"E2"),sQuery(id+"F2.wireOp",EDGE,"E3"),sQuery(id+"F2.wireOp",EDGE,"E4"),sQuery(id+"F2.wireOp",EDGE,"E5.filletArc"),sQuery(id+"F2.wireOp",EDGE,"E6.filletArc"),sQuery(id+"F2.wireOp",EDGE,"E7"),sQuery(id+"F2.wireOp",EDGE,"E8"),sQuery(id+"F2.wireOp",EDGE,"E10")])]}),"instanceName":"126"});
            var Q128;
            Q128=makeQuery(id+"F5.opPattern","COPY",BODY,{"derivedFrom":makeQuery(id+"F3.opExtrude","SWEPT_BODY",BODY,{"disambiguationData":[OSD([sQuery(id+"F2.wireOp",EDGE,"E2"),sQuery(id+"F2.wireOp",EDGE,"E3"),sQuery(id+"F2.wireOp",EDGE,"E4"),sQuery(id+"F2.wireOp",EDGE,"E5.filletArc"),sQuery(id+"F2.wireOp",EDGE,"E6.filletArc"),sQuery(id+"F2.wireOp",EDGE,"E7"),sQuery(id+"F2.wireOp",EDGE,"E8"),sQuery(id+"F2.wireOp",EDGE,"E10")])]}),"instanceName":"127"});
            booleanBodies(context, id + "F6", {"operationType" : BooleanOperationType.UNION, "tools" : qUnion([Q0, Q1, Q2, Q3, Q4, Q5, Q6, Q7, Q8, Q9, Q10, Q11, Q12, Q13, Q14, Q15, Q16, Q17, Q18, Q19, Q20, Q21, Q22, Q23, Q24, Q25, Q26, Q27, Q28, Q29, Q30, Q31, Q32, Q33, Q34, Q35, Q36, Q37, Q38, Q39, Q40, Q41, Q42, Q43, Q44, Q45, Q46, Q47, Q48, Q49, Q50, Q51, Q52, Q53, Q54, Q55, Q56, Q57, Q58, Q59, Q60, Q61, Q62, Q63, Q64, Q65, Q66, Q67, Q68, Q69, Q70, Q71, Q72, Q73, Q74, Q75, Q76, Q77, Q78, Q79, Q80, Q81, Q82, Q83, Q84, Q85, Q86, Q87, Q88, Q89, Q90, Q91, Q92, Q93, Q94, Q95, Q96, Q97, Q98, Q99, Q100, Q101, Q102, Q103, Q104, Q105, Q106, Q107, Q108, Q109, Q110, Q111, Q112, Q113, Q114, Q115, Q116, Q117, Q118, Q119, Q120, Q121, Q122, Q123, Q124, Q125, Q126, Q127, Q128])});
        }
        {
            var Q0;
            {var subQ0=sQuery(id+"F0.wireOp",EDGE,"E0");var subQ1=makeQuery(id+"F3.opExtrude","CAP_FACE",FACE,{"disambiguationData":[OSD([subQ0])],"isStart":false});Q0=makeQuery(id+"F6.opBoolean","MERGE",FACE,{"derivedFrom":[makeQuery(id+"F1.opExtrude","CAP_FACE",FACE,{"disambiguationData":[OSD([subQ0])],"isStart":false}),subQ1,makeQuery(id+"F5.opPattern","COPY",FACE,{"derivedFrom":subQ1,"instanceName":"1"}),makeQuery(id+"F5.opPattern","COPY",FACE,{"derivedFrom":subQ1,"instanceName":"2"}),makeQuery(id+"F5.opPattern","COPY",FACE,{"derivedFrom":subQ1,"instanceName":"3"}),makeQuery(id+"F5.opPattern","COPY",FACE,{"derivedFrom":subQ1,"instanceName":"4"}),makeQuery(id+"F5.opPattern","COPY",FACE,{"derivedFrom":subQ1,"instanceName":"5"}),makeQuery(id+"F5.opPattern","COPY",FACE,{"derivedFrom":subQ1,"instanceName":"6"}),makeQuery(id+"F5.opPattern","COPY",FACE,{"derivedFrom":subQ1,"instanceName":"7"}),makeQuery(id+"F5.opPattern","COPY",FACE,{"derivedFrom":subQ1,"instanceName":"8"}),makeQuery(id+"F5.opPattern","COPY",FACE,{"derivedFrom":subQ1,"instanceName":"9"}),makeQuery(id+"F5.opPattern","COPY",FACE,{"derivedFrom":subQ1,"instanceName":"10"}),makeQuery(id+"F5.opPattern","COPY",FACE,{"derivedFrom":subQ1,"instanceName":"11"}),makeQuery(id+"F5.opPattern","COPY",FACE,{"derivedFrom":subQ1,"instanceName":"12"}),makeQuery(id+"F5.opPattern","COPY",FACE,{"derivedFrom":subQ1,"instanceName":"13"}),makeQuery(id+"F5.opPattern","COPY",FACE,{"derivedFrom":subQ1,"instanceName":"14"}),makeQuery(id+"F5.opPattern","COPY",FACE,{"derivedFrom":subQ1,"instanceName":"15"}),makeQuery(id+"F5.opPattern","COPY",FACE,{"derivedFrom":subQ1,"instanceName":"16"}),makeQuery(id+"F5.opPattern","COPY",FACE,{"derivedFrom":subQ1,"instanceName":"17"}),makeQuery(id+"F5.opPattern","COPY",FACE,{"derivedFrom":subQ1,"instanceName":"18"}),makeQuery(id+"F5.opPattern","COPY",FACE,{"derivedFrom":subQ1,"instanceName":"19"}),makeQuery(id+"F5.opPattern","COPY",FACE,{"derivedFrom":subQ1,"instanceName":"20"}),makeQuery(id+"F5.opPattern","COPY",FACE,{"derivedFrom":subQ1,"instanceName":"21"}),makeQuery(id+"F5.opPattern","COPY",FACE,{"derivedFrom":subQ1,"instanceName":"22"}),makeQuery(id+"F5.opPattern","COPY",FACE,{"derivedFrom":subQ1,"instanceName":"23"}),makeQuery(id+"F5.opPattern","COPY",FACE,{"derivedFrom":subQ1,"instanceName":"24"}),makeQuery(id+"F5.opPattern","COPY",FACE,{"derivedFrom":subQ1,"instanceName":"25"}),makeQuery(id+"F5.opPattern","COPY",FACE,{"derivedFrom":subQ1,"instanceName":"26"}),makeQuery(id+"F5.opPattern","COPY",FACE,{"derivedFrom":subQ1,"instanceName":"27"}),makeQuery(id+"F5.opPattern","COPY",FACE,{"derivedFrom":subQ1,"instanceName":"28"}),makeQuery(id+"F5.opPattern","COPY",FACE,{"derivedFrom":subQ1,"instanceName":"29"}),makeQuery(id+"F5.opPattern","COPY",FACE,{"derivedFrom":subQ1,"instanceName":"30"}),makeQuery(id+"F5.opPattern","COPY",FACE,{"derivedFrom":subQ1,"instanceName":"31"}),makeQuery(id+"F5.opPattern","COPY",FACE,{"derivedFrom":subQ1,"instanceName":"32"}),makeQuery(id+"F5.opPattern","COPY",FACE,{"derivedFrom":subQ1,"instanceName":"33"}),makeQuery(id+"F5.opPattern","COPY",FACE,{"derivedFrom":subQ1,"instanceName":"34"}),makeQuery(id+"F5.opPattern","COPY",FACE,{"derivedFrom":subQ1,"instanceName":"35"}),makeQuery(id+"F5.opPattern","COPY",FACE,{"derivedFrom":subQ1,"instanceName":"36"}),makeQuery(id+"F5.opPattern","COPY",FACE,{"derivedFrom":subQ1,"instanceName":"37"}),makeQuery(id+"F5.opPattern","COPY",FACE,{"derivedFrom":subQ1,"instanceName":"38"}),makeQuery(id+"F5.opPattern","COPY",FACE,{"derivedFrom":subQ1,"instanceName":"39"}),makeQuery(id+"F5.opPattern","COPY",FACE,{"derivedFrom":subQ1,"instanceName":"40"}),makeQuery(id+"F5.opPattern","COPY",FACE,{"derivedFrom":subQ1,"instanceName":"41"}),makeQuery(id+"F5.opPattern","COPY",FACE,{"derivedFrom":subQ1,"instanceName":"42"}),makeQuery(id+"F5.opPattern","COPY",FACE,{"derivedFrom":subQ1,"instanceName":"43"}),makeQuery(id+"F5.opPattern","COPY",FACE,{"derivedFrom":subQ1,"instanceName":"44"}),makeQuery(id+"F5.opPattern","COPY",FACE,{"derivedFrom":subQ1,"instanceName":"45"}),makeQuery(id+"F5.opPattern","COPY",FACE,{"derivedFrom":subQ1,"instanceName":"46"}),makeQuery(id+"F5.opPattern","COPY",FACE,{"derivedFrom":subQ1,"instanceName":"47"}),makeQuery(id+"F5.opPattern","COPY",FACE,{"derivedFrom":subQ1,"instanceName":"48"}),makeQuery(id+"F5.opPattern","COPY",FACE,{"derivedFrom":subQ1,"instanceName":"49"}),makeQuery(id+"F5.opPattern","COPY",FACE,{"derivedFrom":subQ1,"instanceName":"50"}),makeQuery(id+"F5.opPattern","COPY",FACE,{"derivedFrom":subQ1,"instanceName":"51"}),makeQuery(id+"F5.opPattern","COPY",FACE,{"derivedFrom":subQ1,"instanceName":"52"}),makeQuery(id+"F5.opPattern","COPY",FACE,{"derivedFrom":subQ1,"instanceName":"53"}),makeQuery(id+"F5.opPattern","COPY",FACE,{"derivedFrom":subQ1,"instanceName":"54"}),makeQuery(id+"F5.opPattern","COPY",FACE,{"derivedFrom":subQ1,"instanceName":"55"}),makeQuery(id+"F5.opPattern","COPY",FACE,{"derivedFrom":subQ1,"instanceName":"56"}),makeQuery(id+"F5.opPattern","COPY",FACE,{"derivedFrom":subQ1,"instanceName":"57"}),makeQuery(id+"F5.opPattern","COPY",FACE,{"derivedFrom":subQ1,"instanceName":"58"}),makeQuery(id+"F5.opPattern","COPY",FACE,{"derivedFrom":subQ1,"instanceName":"59"}),makeQuery(id+"F5.opPattern","COPY",FACE,{"derivedFrom":subQ1,"instanceName":"60"}),makeQuery(id+"F5.opPattern","COPY",FACE,{"derivedFrom":subQ1,"instanceName":"61"}),makeQuery(id+"F5.opPattern","COPY",FACE,{"derivedFrom":subQ1,"instanceName":"62"}),makeQuery(id+"F5.opPattern","COPY",FACE,{"derivedFrom":subQ1,"instanceName":"63"}),makeQuery(id+"F5.opPattern","COPY",FACE,{"derivedFrom":subQ1,"instanceName":"64"}),makeQuery(id+"F5.opPattern","COPY",FACE,{"derivedFrom":subQ1,"instanceName":"65"}),makeQuery(id+"F5.opPattern","COPY",FACE,{"derivedFrom":subQ1,"instanceName":"66"}),makeQuery(id+"F5.opPattern","COPY",FACE,{"derivedFrom":subQ1,"instanceName":"67"}),makeQuery(id+"F5.opPattern","COPY",FACE,{"derivedFrom":subQ1,"instanceName":"68"}),makeQuery(id+"F5.opPattern","COPY",FACE,{"derivedFrom":subQ1,"instanceName":"69"}),makeQuery(id+"F5.opPattern","COPY",FACE,{"derivedFrom":subQ1,"instanceName":"70"}),makeQuery(id+"F5.opPattern","COPY",FACE,{"derivedFrom":subQ1,"instanceName":"71"}),makeQuery(id+"F5.opPattern","COPY",FACE,{"derivedFrom":subQ1,"instanceName":"72"}),makeQuery(id+"F5.opPattern","COPY",FACE,{"derivedFrom":subQ1,"instanceName":"73"}),makeQuery(id+"F5.opPattern","COPY",FACE,{"derivedFrom":subQ1,"instanceName":"74"}),makeQuery(id+"F5.opPattern","COPY",FACE,{"derivedFrom":subQ1,"instanceName":"75"}),makeQuery(id+"F5.opPattern","COPY",FACE,{"derivedFrom":subQ1,"instanceName":"76"}),makeQuery(id+"F5.opPattern","COPY",FACE,{"derivedFrom":subQ1,"instanceName":"77"}),makeQuery(id+"F5.opPattern","COPY",FACE,{"derivedFrom":subQ1,"instanceName":"78"}),makeQuery(id+"F5.opPattern","COPY",FACE,{"derivedFrom":subQ1,"instanceName":"79"}),makeQuery(id+"F5.opPattern","COPY",FACE,{"derivedFrom":subQ1,"instanceName":"80"}),makeQuery(id+"F5.opPattern","COPY",FACE,{"derivedFrom":subQ1,"instanceName":"81"}),makeQuery(id+"F5.opPattern","COPY",FACE,{"derivedFrom":subQ1,"instanceName":"82"}),makeQuery(id+"F5.opPattern","COPY",FACE,{"derivedFrom":subQ1,"instanceName":"83"}),makeQuery(id+"F5.opPattern","COPY",FACE,{"derivedFrom":subQ1,"instanceName":"84"}),makeQuery(id+"F5.opPattern","COPY",FACE,{"derivedFrom":subQ1,"instanceName":"85"}),makeQuery(id+"F5.opPattern","COPY",FACE,{"derivedFrom":subQ1,"instanceName":"86"}),makeQuery(id+"F5.opPattern","COPY",FACE,{"derivedFrom":subQ1,"instanceName":"87"}),makeQuery(id+"F5.opPattern","COPY",FACE,{"derivedFrom":subQ1,"instanceName":"88"}),makeQuery(id+"F5.opPattern","COPY",FACE,{"derivedFrom":subQ1,"instanceName":"89"}),makeQuery(id+"F5.opPattern","COPY",FACE,{"derivedFrom":subQ1,"instanceName":"90"}),makeQuery(id+"F5.opPattern","COPY",FACE,{"derivedFrom":subQ1,"instanceName":"91"}),makeQuery(id+"F5.opPattern","COPY",FACE,{"derivedFrom":subQ1,"instanceName":"92"}),makeQuery(id+"F5.opPattern","COPY",FACE,{"derivedFrom":subQ1,"instanceName":"93"}),makeQuery(id+"F5.opPattern","COPY",FACE,{"derivedFrom":subQ1,"instanceName":"94"}),makeQuery(id+"F5.opPattern","COPY",FACE,{"derivedFrom":subQ1,"instanceName":"95"}),makeQuery(id+"F5.opPattern","COPY",FACE,{"derivedFrom":subQ1,"instanceName":"96"}),makeQuery(id+"F5.opPattern","COPY",FACE,{"derivedFrom":subQ1,"instanceName":"97"}),makeQuery(id+"F5.opPattern","COPY",FACE,{"derivedFrom":subQ1,"instanceName":"98"}),makeQuery(id+"F5.opPattern","COPY",FACE,{"derivedFrom":subQ1,"instanceName":"99"}),makeQuery(id+"F5.opPattern","COPY",FACE,{"derivedFrom":subQ1,"instanceName":"100"}),makeQuery(id+"F5.opPattern","COPY",FACE,{"derivedFrom":subQ1,"instanceName":"101"}),makeQuery(id+"F5.opPattern","COPY",FACE,{"derivedFrom":subQ1,"instanceName":"102"}),makeQuery(id+"F5.opPattern","COPY",FACE,{"derivedFrom":subQ1,"instanceName":"103"}),makeQuery(id+"F5.opPattern","COPY",FACE,{"derivedFrom":subQ1,"instanceName":"104"}),makeQuery(id+"F5.opPattern","COPY",FACE,{"derivedFrom":subQ1,"instanceName":"105"}),makeQuery(id+"F5.opPattern","COPY",FACE,{"derivedFrom":subQ1,"instanceName":"106"}),makeQuery(id+"F5.opPattern","COPY",FACE,{"derivedFrom":subQ1,"instanceName":"107"}),makeQuery(id+"F5.opPattern","COPY",FACE,{"derivedFrom":subQ1,"instanceName":"108"}),makeQuery(id+"F5.opPattern","COPY",FACE,{"derivedFrom":subQ1,"instanceName":"109"}),makeQuery(id+"F5.opPattern","COPY",FACE,{"derivedFrom":subQ1,"instanceName":"110"}),makeQuery(id+"F5.opPattern","COPY",FACE,{"derivedFrom":subQ1,"instanceName":"111"}),makeQuery(id+"F5.opPattern","COPY",FACE,{"derivedFrom":subQ1,"instanceName":"112"}),makeQuery(id+"F5.opPattern","COPY",FACE,{"derivedFrom":subQ1,"instanceName":"113"}),makeQuery(id+"F5.opPattern","COPY",FACE,{"derivedFrom":subQ1,"instanceName":"114"}),makeQuery(id+"F5.opPattern","COPY",FACE,{"derivedFrom":subQ1,"instanceName":"115"}),makeQuery(id+"F5.opPattern","COPY",FACE,{"derivedFrom":subQ1,"instanceName":"116"}),makeQuery(id+"F5.opPattern","COPY",FACE,{"derivedFrom":subQ1,"instanceName":"117"}),makeQuery(id+"F5.opPattern","COPY",FACE,{"derivedFrom":subQ1,"instanceName":"118"}),makeQuery(id+"F5.opPattern","COPY",FACE,{"derivedFrom":subQ1,"instanceName":"119"}),makeQuery(id+"F5.opPattern","COPY",FACE,{"derivedFrom":subQ1,"instanceName":"120"}),makeQuery(id+"F5.opPattern","COPY",FACE,{"derivedFrom":subQ1,"instanceName":"121"}),makeQuery(id+"F5.opPattern","COPY",FACE,{"derivedFrom":subQ1,"instanceName":"122"}),makeQuery(id+"F5.opPattern","COPY",FACE,{"derivedFrom":subQ1,"instanceName":"123"}),makeQuery(id+"F5.opPattern","COPY",FACE,{"derivedFrom":subQ1,"instanceName":"124"}),makeQuery(id+"F5.opPattern","COPY",FACE,{"derivedFrom":subQ1,"instanceName":"125"}),makeQuery(id+"F5.opPattern","COPY",FACE,{"derivedFrom":subQ1,"instanceName":"126"}),makeQuery(id+"F5.opPattern","COPY",FACE,{"derivedFrom":subQ1,"instanceName":"127"})]});}
            var sketch = newSketch(context, id + "F7", { "sketchPlane" : qUnion([Q0])});
            skCircle(sketch, "E12", {"center": v(0, 0) * mm, "radius": 30.23 * mm});
            skSolve(sketch);
        }
        {
            var Q0;
            Q0=qSketchRegion(id+"F7",true);
            extrude(context, id + "F8", {"entities" : qUnion([Q0]), "operationType" : NewBodyOperationType.REMOVE, "oppositeDirection" : true, "depth" : 25.4 * mm});
        }
        {
            var Q0;
            {var subQ0=makeQuery(id+"F3.opExtrude","CAP_FACE",FACE,{"disambiguationData":[OSD([sQuery(id+"F2.wireOp",EDGE,"E2"),sQuery(id+"F2.wireOp",EDGE,"E3"),sQuery(id+"F2.wireOp",EDGE,"E4"),sQuery(id+"F2.wireOp",EDGE,"E5.filletArc"),sQuery(id+"F2.wireOp",EDGE,"E6.filletArc"),sQuery(id+"F2.wireOp",EDGE,"E7"),sQuery(id+"F2.wireOp",EDGE,"E8"),sQuery(id+"F2.wireOp",EDGE,"E10")])],"isStart":true});Q0=makeQuery(id+"F6.opBoolean","MERGE",FACE,{"derivedFrom":[makeQuery(id+"F1.opExtrude","CAP_FACE",FACE,{"disambiguationData":[OSD([sQuery(id+"F0.wireOp",EDGE,"E0")])],"isStart":true}),subQ0,makeQuery(id+"F5.opPattern","COPY",FACE,{"derivedFrom":subQ0,"instanceName":"1"}),makeQuery(id+"F5.opPattern","COPY",FACE,{"derivedFrom":subQ0,"instanceName":"2"}),makeQuery(id+"F5.opPattern","COPY",FACE,{"derivedFrom":subQ0,"instanceName":"3"}),makeQuery(id+"F5.opPattern","COPY",FACE,{"derivedFrom":subQ0,"instanceName":"4"}),makeQuery(id+"F5.opPattern","COPY",FACE,{"derivedFrom":subQ0,"instanceName":"5"}),makeQuery(id+"F5.opPattern","COPY",FACE,{"derivedFrom":subQ0,"instanceName":"6"}),makeQuery(id+"F5.opPattern","COPY",FACE,{"derivedFrom":subQ0,"instanceName":"7"}),makeQuery(id+"F5.opPattern","COPY",FACE,{"derivedFrom":subQ0,"instanceName":"8"}),makeQuery(id+"F5.opPattern","COPY",FACE,{"derivedFrom":subQ0,"instanceName":"9"}),makeQuery(id+"F5.opPattern","COPY",FACE,{"derivedFrom":subQ0,"instanceName":"10"}),makeQuery(id+"F5.opPattern","COPY",FACE,{"derivedFrom":subQ0,"instanceName":"11"}),makeQuery(id+"F5.opPattern","COPY",FACE,{"derivedFrom":subQ0,"instanceName":"12"}),makeQuery(id+"F5.opPattern","COPY",FACE,{"derivedFrom":subQ0,"instanceName":"13"}),makeQuery(id+"F5.opPattern","COPY",FACE,{"derivedFrom":subQ0,"instanceName":"14"}),makeQuery(id+"F5.opPattern","COPY",FACE,{"derivedFrom":subQ0,"instanceName":"15"}),makeQuery(id+"F5.opPattern","COPY",FACE,{"derivedFrom":subQ0,"instanceName":"16"}),makeQuery(id+"F5.opPattern","COPY",FACE,{"derivedFrom":subQ0,"instanceName":"17"}),makeQuery(id+"F5.opPattern","COPY",FACE,{"derivedFrom":subQ0,"instanceName":"18"}),makeQuery(id+"F5.opPattern","COPY",FACE,{"derivedFrom":subQ0,"instanceName":"19"}),makeQuery(id+"F5.opPattern","COPY",FACE,{"derivedFrom":subQ0,"instanceName":"20"}),makeQuery(id+"F5.opPattern","COPY",FACE,{"derivedFrom":subQ0,"instanceName":"21"}),makeQuery(id+"F5.opPattern","COPY",FACE,{"derivedFrom":subQ0,"instanceName":"22"}),makeQuery(id+"F5.opPattern","COPY",FACE,{"derivedFrom":subQ0,"instanceName":"23"}),makeQuery(id+"F5.opPattern","COPY",FACE,{"derivedFrom":subQ0,"instanceName":"24"}),makeQuery(id+"F5.opPattern","COPY",FACE,{"derivedFrom":subQ0,"instanceName":"25"}),makeQuery(id+"F5.opPattern","COPY",FACE,{"derivedFrom":subQ0,"instanceName":"26"}),makeQuery(id+"F5.opPattern","COPY",FACE,{"derivedFrom":subQ0,"instanceName":"27"}),makeQuery(id+"F5.opPattern","COPY",FACE,{"derivedFrom":subQ0,"instanceName":"28"}),makeQuery(id+"F5.opPattern","COPY",FACE,{"derivedFrom":subQ0,"instanceName":"29"}),makeQuery(id+"F5.opPattern","COPY",FACE,{"derivedFrom":subQ0,"instanceName":"30"}),makeQuery(id+"F5.opPattern","COPY",FACE,{"derivedFrom":subQ0,"instanceName":"31"}),makeQuery(id+"F5.opPattern","COPY",FACE,{"derivedFrom":subQ0,"instanceName":"32"}),makeQuery(id+"F5.opPattern","COPY",FACE,{"derivedFrom":subQ0,"instanceName":"33"}),makeQuery(id+"F5.opPattern","COPY",FACE,{"derivedFrom":subQ0,"instanceName":"34"}),makeQuery(id+"F5.opPattern","COPY",FACE,{"derivedFrom":subQ0,"instanceName":"35"}),makeQuery(id+"F5.opPattern","COPY",FACE,{"derivedFrom":subQ0,"instanceName":"36"}),makeQuery(id+"F5.opPattern","COPY",FACE,{"derivedFrom":subQ0,"instanceName":"37"}),makeQuery(id+"F5.opPattern","COPY",FACE,{"derivedFrom":subQ0,"instanceName":"38"}),makeQuery(id+"F5.opPattern","COPY",FACE,{"derivedFrom":subQ0,"instanceName":"39"}),makeQuery(id+"F5.opPattern","COPY",FACE,{"derivedFrom":subQ0,"instanceName":"40"}),makeQuery(id+"F5.opPattern","COPY",FACE,{"derivedFrom":subQ0,"instanceName":"41"}),makeQuery(id+"F5.opPattern","COPY",FACE,{"derivedFrom":subQ0,"instanceName":"42"}),makeQuery(id+"F5.opPattern","COPY",FACE,{"derivedFrom":subQ0,"instanceName":"43"}),makeQuery(id+"F5.opPattern","COPY",FACE,{"derivedFrom":subQ0,"instanceName":"44"}),makeQuery(id+"F5.opPattern","COPY",FACE,{"derivedFrom":subQ0,"instanceName":"45"}),makeQuery(id+"F5.opPattern","COPY",FACE,{"derivedFrom":subQ0,"instanceName":"46"}),makeQuery(id+"F5.opPattern","COPY",FACE,{"derivedFrom":subQ0,"instanceName":"47"}),makeQuery(id+"F5.opPattern","COPY",FACE,{"derivedFrom":subQ0,"instanceName":"48"}),makeQuery(id+"F5.opPattern","COPY",FACE,{"derivedFrom":subQ0,"instanceName":"49"}),makeQuery(id+"F5.opPattern","COPY",FACE,{"derivedFrom":subQ0,"instanceName":"50"}),makeQuery(id+"F5.opPattern","COPY",FACE,{"derivedFrom":subQ0,"instanceName":"51"}),makeQuery(id+"F5.opPattern","COPY",FACE,{"derivedFrom":subQ0,"instanceName":"52"}),makeQuery(id+"F5.opPattern","COPY",FACE,{"derivedFrom":subQ0,"instanceName":"53"}),makeQuery(id+"F5.opPattern","COPY",FACE,{"derivedFrom":subQ0,"instanceName":"54"}),makeQuery(id+"F5.opPattern","COPY",FACE,{"derivedFrom":subQ0,"instanceName":"55"}),makeQuery(id+"F5.opPattern","COPY",FACE,{"derivedFrom":subQ0,"instanceName":"56"}),makeQuery(id+"F5.opPattern","COPY",FACE,{"derivedFrom":subQ0,"instanceName":"57"}),makeQuery(id+"F5.opPattern","COPY",FACE,{"derivedFrom":subQ0,"instanceName":"58"}),makeQuery(id+"F5.opPattern","COPY",FACE,{"derivedFrom":subQ0,"instanceName":"59"}),makeQuery(id+"F5.opPattern","COPY",FACE,{"derivedFrom":subQ0,"instanceName":"60"}),makeQuery(id+"F5.opPattern","COPY",FACE,{"derivedFrom":subQ0,"instanceName":"61"}),makeQuery(id+"F5.opPattern","COPY",FACE,{"derivedFrom":subQ0,"instanceName":"62"}),makeQuery(id+"F5.opPattern","COPY",FACE,{"derivedFrom":subQ0,"instanceName":"63"}),makeQuery(id+"F5.opPattern","COPY",FACE,{"derivedFrom":subQ0,"instanceName":"64"}),makeQuery(id+"F5.opPattern","COPY",FACE,{"derivedFrom":subQ0,"instanceName":"65"}),makeQuery(id+"F5.opPattern","COPY",FACE,{"derivedFrom":subQ0,"instanceName":"66"}),makeQuery(id+"F5.opPattern","COPY",FACE,{"derivedFrom":subQ0,"instanceName":"67"}),makeQuery(id+"F5.opPattern","COPY",FACE,{"derivedFrom":subQ0,"instanceName":"68"}),makeQuery(id+"F5.opPattern","COPY",FACE,{"derivedFrom":subQ0,"instanceName":"69"}),makeQuery(id+"F5.opPattern","COPY",FACE,{"derivedFrom":subQ0,"instanceName":"70"}),makeQuery(id+"F5.opPattern","COPY",FACE,{"derivedFrom":subQ0,"instanceName":"71"}),makeQuery(id+"F5.opPattern","COPY",FACE,{"derivedFrom":subQ0,"instanceName":"72"}),makeQuery(id+"F5.opPattern","COPY",FACE,{"derivedFrom":subQ0,"instanceName":"73"}),makeQuery(id+"F5.opPattern","COPY",FACE,{"derivedFrom":subQ0,"instanceName":"74"}),makeQuery(id+"F5.opPattern","COPY",FACE,{"derivedFrom":subQ0,"instanceName":"75"}),makeQuery(id+"F5.opPattern","COPY",FACE,{"derivedFrom":subQ0,"instanceName":"76"}),makeQuery(id+"F5.opPattern","COPY",FACE,{"derivedFrom":subQ0,"instanceName":"77"}),makeQuery(id+"F5.opPattern","COPY",FACE,{"derivedFrom":subQ0,"instanceName":"78"}),makeQuery(id+"F5.opPattern","COPY",FACE,{"derivedFrom":subQ0,"instanceName":"79"}),makeQuery(id+"F5.opPattern","COPY",FACE,{"derivedFrom":subQ0,"instanceName":"80"}),makeQuery(id+"F5.opPattern","COPY",FACE,{"derivedFrom":subQ0,"instanceName":"81"}),makeQuery(id+"F5.opPattern","COPY",FACE,{"derivedFrom":subQ0,"instanceName":"82"}),makeQuery(id+"F5.opPattern","COPY",FACE,{"derivedFrom":subQ0,"instanceName":"83"}),makeQuery(id+"F5.opPattern","COPY",FACE,{"derivedFrom":subQ0,"instanceName":"84"}),makeQuery(id+"F5.opPattern","COPY",FACE,{"derivedFrom":subQ0,"instanceName":"85"}),makeQuery(id+"F5.opPattern","COPY",FACE,{"derivedFrom":subQ0,"instanceName":"86"}),makeQuery(id+"F5.opPattern","COPY",FACE,{"derivedFrom":subQ0,"instanceName":"87"}),makeQuery(id+"F5.opPattern","COPY",FACE,{"derivedFrom":subQ0,"instanceName":"88"}),makeQuery(id+"F5.opPattern","COPY",FACE,{"derivedFrom":subQ0,"instanceName":"89"}),makeQuery(id+"F5.opPattern","COPY",FACE,{"derivedFrom":subQ0,"instanceName":"90"}),makeQuery(id+"F5.opPattern","COPY",FACE,{"derivedFrom":subQ0,"instanceName":"91"}),makeQuery(id+"F5.opPattern","COPY",FACE,{"derivedFrom":subQ0,"instanceName":"92"}),makeQuery(id+"F5.opPattern","COPY",FACE,{"derivedFrom":subQ0,"instanceName":"93"}),makeQuery(id+"F5.opPattern","COPY",FACE,{"derivedFrom":subQ0,"instanceName":"94"}),makeQuery(id+"F5.opPattern","COPY",FACE,{"derivedFrom":subQ0,"instanceName":"95"}),makeQuery(id+"F5.opPattern","COPY",FACE,{"derivedFrom":subQ0,"instanceName":"96"}),makeQuery(id+"F5.opPattern","COPY",FACE,{"derivedFrom":subQ0,"instanceName":"97"}),makeQuery(id+"F5.opPattern","COPY",FACE,{"derivedFrom":subQ0,"instanceName":"98"}),makeQuery(id+"F5.opPattern","COPY",FACE,{"derivedFrom":subQ0,"instanceName":"99"}),makeQuery(id+"F5.opPattern","COPY",FACE,{"derivedFrom":subQ0,"instanceName":"100"}),makeQuery(id+"F5.opPattern","COPY",FACE,{"derivedFrom":subQ0,"instanceName":"101"}),makeQuery(id+"F5.opPattern","COPY",FACE,{"derivedFrom":subQ0,"instanceName":"102"}),makeQuery(id+"F5.opPattern","COPY",FACE,{"derivedFrom":subQ0,"instanceName":"103"}),makeQuery(id+"F5.opPattern","COPY",FACE,{"derivedFrom":subQ0,"instanceName":"104"}),makeQuery(id+"F5.opPattern","COPY",FACE,{"derivedFrom":subQ0,"instanceName":"105"}),makeQuery(id+"F5.opPattern","COPY",FACE,{"derivedFrom":subQ0,"instanceName":"106"}),makeQuery(id+"F5.opPattern","COPY",FACE,{"derivedFrom":subQ0,"instanceName":"107"}),makeQuery(id+"F5.opPattern","COPY",FACE,{"derivedFrom":subQ0,"instanceName":"108"}),makeQuery(id+"F5.opPattern","COPY",FACE,{"derivedFrom":subQ0,"instanceName":"109"}),makeQuery(id+"F5.opPattern","COPY",FACE,{"derivedFrom":subQ0,"instanceName":"110"}),makeQuery(id+"F5.opPattern","COPY",FACE,{"derivedFrom":subQ0,"instanceName":"111"}),makeQuery(id+"F5.opPattern","COPY",FACE,{"derivedFrom":subQ0,"instanceName":"112"}),makeQuery(id+"F5.opPattern","COPY",FACE,{"derivedFrom":subQ0,"instanceName":"113"}),makeQuery(id+"F5.opPattern","COPY",FACE,{"derivedFrom":subQ0,"instanceName":"114"}),makeQuery(id+"F5.opPattern","COPY",FACE,{"derivedFrom":subQ0,"instanceName":"115"}),makeQuery(id+"F5.opPattern","COPY",FACE,{"derivedFrom":subQ0,"instanceName":"116"}),makeQuery(id+"F5.opPattern","COPY",FACE,{"derivedFrom":subQ0,"instanceName":"117"}),makeQuery(id+"F5.opPattern","COPY",FACE,{"derivedFrom":subQ0,"instanceName":"118"}),makeQuery(id+"F5.opPattern","COPY",FACE,{"derivedFrom":subQ0,"instanceName":"119"}),makeQuery(id+"F5.opPattern","COPY",FACE,{"derivedFrom":subQ0,"instanceName":"120"}),makeQuery(id+"F5.opPattern","COPY",FACE,{"derivedFrom":subQ0,"instanceName":"121"}),makeQuery(id+"F5.opPattern","COPY",FACE,{"derivedFrom":subQ0,"instanceName":"122"}),makeQuery(id+"F5.opPattern","COPY",FACE,{"derivedFrom":subQ0,"instanceName":"123"}),makeQuery(id+"F5.opPattern","COPY",FACE,{"derivedFrom":subQ0,"instanceName":"124"}),makeQuery(id+"F5.opPattern","COPY",FACE,{"derivedFrom":subQ0,"instanceName":"125"}),makeQuery(id+"F5.opPattern","COPY",FACE,{"derivedFrom":subQ0,"instanceName":"126"}),makeQuery(id+"F5.opPattern","COPY",FACE,{"derivedFrom":subQ0,"instanceName":"127"})]});}
            var sketch = newSketch(context, id + "F9", { "sketchPlane" : qUnion([Q0])});
            skCircle(sketch, "E13", {"center": v(0, 0) * mm, "radius": 155.58 * mm});
            skCircle(sketch, "E14.0", {"center": v(0, 0) * mm, "radius": 30.23 * mm});
            skSolve(sketch);
        }
        {
            var Q0;
            Q0=qSketchRegion(id+"F9",true);
            extrude(context, id + "F10", {"entities" : qUnion([Q0]), "operationType" : NewBodyOperationType.ADD, "depth" : 17.53 * mm});
        }
        {
            var Q0;
            {var subQ0=sQuery(id+"F0.wireOp",EDGE,"E0");var subQ1=makeQuery(id+"F3.opExtrude","CAP_FACE",FACE,{"disambiguationData":[OSD([subQ0])],"isStart":false});Q0=makeQuery(id+"F6.opBoolean","MERGE",FACE,{"derivedFrom":[makeQuery(id+"F1.opExtrude","CAP_FACE",FACE,{"disambiguationData":[OSD([subQ0])],"isStart":false}),subQ1,makeQuery(id+"F5.opPattern","COPY",FACE,{"derivedFrom":subQ1,"instanceName":"1"}),makeQuery(id+"F5.opPattern","COPY",FACE,{"derivedFrom":subQ1,"instanceName":"2"}),makeQuery(id+"F5.opPattern","COPY",FACE,{"derivedFrom":subQ1,"instanceName":"3"}),makeQuery(id+"F5.opPattern","COPY",FACE,{"derivedFrom":subQ1,"instanceName":"4"}),makeQuery(id+"F5.opPattern","COPY",FACE,{"derivedFrom":subQ1,"instanceName":"5"}),makeQuery(id+"F5.opPattern","COPY",FACE,{"derivedFrom":subQ1,"instanceName":"6"}),makeQuery(id+"F5.opPattern","COPY",FACE,{"derivedFrom":subQ1,"instanceName":"7"}),makeQuery(id+"F5.opPattern","COPY",FACE,{"derivedFrom":subQ1,"instanceName":"8"}),makeQuery(id+"F5.opPattern","COPY",FACE,{"derivedFrom":subQ1,"instanceName":"9"}),makeQuery(id+"F5.opPattern","COPY",FACE,{"derivedFrom":subQ1,"instanceName":"10"}),makeQuery(id+"F5.opPattern","COPY",FACE,{"derivedFrom":subQ1,"instanceName":"11"}),makeQuery(id+"F5.opPattern","COPY",FACE,{"derivedFrom":subQ1,"instanceName":"12"}),makeQuery(id+"F5.opPattern","COPY",FACE,{"derivedFrom":subQ1,"instanceName":"13"}),makeQuery(id+"F5.opPattern","COPY",FACE,{"derivedFrom":subQ1,"instanceName":"14"}),makeQuery(id+"F5.opPattern","COPY",FACE,{"derivedFrom":subQ1,"instanceName":"15"}),makeQuery(id+"F5.opPattern","COPY",FACE,{"derivedFrom":subQ1,"instanceName":"16"}),makeQuery(id+"F5.opPattern","COPY",FACE,{"derivedFrom":subQ1,"instanceName":"17"}),makeQuery(id+"F5.opPattern","COPY",FACE,{"derivedFrom":subQ1,"instanceName":"18"}),makeQuery(id+"F5.opPattern","COPY",FACE,{"derivedFrom":subQ1,"instanceName":"19"}),makeQuery(id+"F5.opPattern","COPY",FACE,{"derivedFrom":subQ1,"instanceName":"20"}),makeQuery(id+"F5.opPattern","COPY",FACE,{"derivedFrom":subQ1,"instanceName":"21"}),makeQuery(id+"F5.opPattern","COPY",FACE,{"derivedFrom":subQ1,"instanceName":"22"}),makeQuery(id+"F5.opPattern","COPY",FACE,{"derivedFrom":subQ1,"instanceName":"23"}),makeQuery(id+"F5.opPattern","COPY",FACE,{"derivedFrom":subQ1,"instanceName":"24"}),makeQuery(id+"F5.opPattern","COPY",FACE,{"derivedFrom":subQ1,"instanceName":"25"}),makeQuery(id+"F5.opPattern","COPY",FACE,{"derivedFrom":subQ1,"instanceName":"26"}),makeQuery(id+"F5.opPattern","COPY",FACE,{"derivedFrom":subQ1,"instanceName":"27"}),makeQuery(id+"F5.opPattern","COPY",FACE,{"derivedFrom":subQ1,"instanceName":"28"}),makeQuery(id+"F5.opPattern","COPY",FACE,{"derivedFrom":subQ1,"instanceName":"29"}),makeQuery(id+"F5.opPattern","COPY",FACE,{"derivedFrom":subQ1,"instanceName":"30"}),makeQuery(id+"F5.opPattern","COPY",FACE,{"derivedFrom":subQ1,"instanceName":"31"}),makeQuery(id+"F5.opPattern","COPY",FACE,{"derivedFrom":subQ1,"instanceName":"32"}),makeQuery(id+"F5.opPattern","COPY",FACE,{"derivedFrom":subQ1,"instanceName":"33"}),makeQuery(id+"F5.opPattern","COPY",FACE,{"derivedFrom":subQ1,"instanceName":"34"}),makeQuery(id+"F5.opPattern","COPY",FACE,{"derivedFrom":subQ1,"instanceName":"35"}),makeQuery(id+"F5.opPattern","COPY",FACE,{"derivedFrom":subQ1,"instanceName":"36"}),makeQuery(id+"F5.opPattern","COPY",FACE,{"derivedFrom":subQ1,"instanceName":"37"}),makeQuery(id+"F5.opPattern","COPY",FACE,{"derivedFrom":subQ1,"instanceName":"38"}),makeQuery(id+"F5.opPattern","COPY",FACE,{"derivedFrom":subQ1,"instanceName":"39"}),makeQuery(id+"F5.opPattern","COPY",FACE,{"derivedFrom":subQ1,"instanceName":"40"}),makeQuery(id+"F5.opPattern","COPY",FACE,{"derivedFrom":subQ1,"instanceName":"41"}),makeQuery(id+"F5.opPattern","COPY",FACE,{"derivedFrom":subQ1,"instanceName":"42"}),makeQuery(id+"F5.opPattern","COPY",FACE,{"derivedFrom":subQ1,"instanceName":"43"}),makeQuery(id+"F5.opPattern","COPY",FACE,{"derivedFrom":subQ1,"instanceName":"44"}),makeQuery(id+"F5.opPattern","COPY",FACE,{"derivedFrom":subQ1,"instanceName":"45"}),makeQuery(id+"F5.opPattern","COPY",FACE,{"derivedFrom":subQ1,"instanceName":"46"}),makeQuery(id+"F5.opPattern","COPY",FACE,{"derivedFrom":subQ1,"instanceName":"47"}),makeQuery(id+"F5.opPattern","COPY",FACE,{"derivedFrom":subQ1,"instanceName":"48"}),makeQuery(id+"F5.opPattern","COPY",FACE,{"derivedFrom":subQ1,"instanceName":"49"}),makeQuery(id+"F5.opPattern","COPY",FACE,{"derivedFrom":subQ1,"instanceName":"50"}),makeQuery(id+"F5.opPattern","COPY",FACE,{"derivedFrom":subQ1,"instanceName":"51"}),makeQuery(id+"F5.opPattern","COPY",FACE,{"derivedFrom":subQ1,"instanceName":"52"}),makeQuery(id+"F5.opPattern","COPY",FACE,{"derivedFrom":subQ1,"instanceName":"53"}),makeQuery(id+"F5.opPattern","COPY",FACE,{"derivedFrom":subQ1,"instanceName":"54"}),makeQuery(id+"F5.opPattern","COPY",FACE,{"derivedFrom":subQ1,"instanceName":"55"}),makeQuery(id+"F5.opPattern","COPY",FACE,{"derivedFrom":subQ1,"instanceName":"56"}),makeQuery(id+"F5.opPattern","COPY",FACE,{"derivedFrom":subQ1,"instanceName":"57"}),makeQuery(id+"F5.opPattern","COPY",FACE,{"derivedFrom":subQ1,"instanceName":"58"}),makeQuery(id+"F5.opPattern","COPY",FACE,{"derivedFrom":subQ1,"instanceName":"59"}),makeQuery(id+"F5.opPattern","COPY",FACE,{"derivedFrom":subQ1,"instanceName":"60"}),makeQuery(id+"F5.opPattern","COPY",FACE,{"derivedFrom":subQ1,"instanceName":"61"}),makeQuery(id+"F5.opPattern","COPY",FACE,{"derivedFrom":subQ1,"instanceName":"62"}),makeQuery(id+"F5.opPattern","COPY",FACE,{"derivedFrom":subQ1,"instanceName":"63"}),makeQuery(id+"F5.opPattern","COPY",FACE,{"derivedFrom":subQ1,"instanceName":"64"}),makeQuery(id+"F5.opPattern","COPY",FACE,{"derivedFrom":subQ1,"instanceName":"65"}),makeQuery(id+"F5.opPattern","COPY",FACE,{"derivedFrom":subQ1,"instanceName":"66"}),makeQuery(id+"F5.opPattern","COPY",FACE,{"derivedFrom":subQ1,"instanceName":"67"}),makeQuery(id+"F5.opPattern","COPY",FACE,{"derivedFrom":subQ1,"instanceName":"68"}),makeQuery(id+"F5.opPattern","COPY",FACE,{"derivedFrom":subQ1,"instanceName":"69"}),makeQuery(id+"F5.opPattern","COPY",FACE,{"derivedFrom":subQ1,"instanceName":"70"}),makeQuery(id+"F5.opPattern","COPY",FACE,{"derivedFrom":subQ1,"instanceName":"71"}),makeQuery(id+"F5.opPattern","COPY",FACE,{"derivedFrom":subQ1,"instanceName":"72"}),makeQuery(id+"F5.opPattern","COPY",FACE,{"derivedFrom":subQ1,"instanceName":"73"}),makeQuery(id+"F5.opPattern","COPY",FACE,{"derivedFrom":subQ1,"instanceName":"74"}),makeQuery(id+"F5.opPattern","COPY",FACE,{"derivedFrom":subQ1,"instanceName":"75"}),makeQuery(id+"F5.opPattern","COPY",FACE,{"derivedFrom":subQ1,"instanceName":"76"}),makeQuery(id+"F5.opPattern","COPY",FACE,{"derivedFrom":subQ1,"instanceName":"77"}),makeQuery(id+"F5.opPattern","COPY",FACE,{"derivedFrom":subQ1,"instanceName":"78"}),makeQuery(id+"F5.opPattern","COPY",FACE,{"derivedFrom":subQ1,"instanceName":"79"}),makeQuery(id+"F5.opPattern","COPY",FACE,{"derivedFrom":subQ1,"instanceName":"80"}),makeQuery(id+"F5.opPattern","COPY",FACE,{"derivedFrom":subQ1,"instanceName":"81"}),makeQuery(id+"F5.opPattern","COPY",FACE,{"derivedFrom":subQ1,"instanceName":"82"}),makeQuery(id+"F5.opPattern","COPY",FACE,{"derivedFrom":subQ1,"instanceName":"83"}),makeQuery(id+"F5.opPattern","COPY",FACE,{"derivedFrom":subQ1,"instanceName":"84"}),makeQuery(id+"F5.opPattern","COPY",FACE,{"derivedFrom":subQ1,"instanceName":"85"}),makeQuery(id+"F5.opPattern","COPY",FACE,{"derivedFrom":subQ1,"instanceName":"86"}),makeQuery(id+"F5.opPattern","COPY",FACE,{"derivedFrom":subQ1,"instanceName":"87"}),makeQuery(id+"F5.opPattern","COPY",FACE,{"derivedFrom":subQ1,"instanceName":"88"}),makeQuery(id+"F5.opPattern","COPY",FACE,{"derivedFrom":subQ1,"instanceName":"89"}),makeQuery(id+"F5.opPattern","COPY",FACE,{"derivedFrom":subQ1,"instanceName":"90"}),makeQuery(id+"F5.opPattern","COPY",FACE,{"derivedFrom":subQ1,"instanceName":"91"}),makeQuery(id+"F5.opPattern","COPY",FACE,{"derivedFrom":subQ1,"instanceName":"92"}),makeQuery(id+"F5.opPattern","COPY",FACE,{"derivedFrom":subQ1,"instanceName":"93"}),makeQuery(id+"F5.opPattern","COPY",FACE,{"derivedFrom":subQ1,"instanceName":"94"}),makeQuery(id+"F5.opPattern","COPY",FACE,{"derivedFrom":subQ1,"instanceName":"95"}),makeQuery(id+"F5.opPattern","COPY",FACE,{"derivedFrom":subQ1,"instanceName":"96"}),makeQuery(id+"F5.opPattern","COPY",FACE,{"derivedFrom":subQ1,"instanceName":"97"}),makeQuery(id+"F5.opPattern","COPY",FACE,{"derivedFrom":subQ1,"instanceName":"98"}),makeQuery(id+"F5.opPattern","COPY",FACE,{"derivedFrom":subQ1,"instanceName":"99"}),makeQuery(id+"F5.opPattern","COPY",FACE,{"derivedFrom":subQ1,"instanceName":"100"}),makeQuery(id+"F5.opPattern","COPY",FACE,{"derivedFrom":subQ1,"instanceName":"101"}),makeQuery(id+"F5.opPattern","COPY",FACE,{"derivedFrom":subQ1,"instanceName":"102"}),makeQuery(id+"F5.opPattern","COPY",FACE,{"derivedFrom":subQ1,"instanceName":"103"}),makeQuery(id+"F5.opPattern","COPY",FACE,{"derivedFrom":subQ1,"instanceName":"104"}),makeQuery(id+"F5.opPattern","COPY",FACE,{"derivedFrom":subQ1,"instanceName":"105"}),makeQuery(id+"F5.opPattern","COPY",FACE,{"derivedFrom":subQ1,"instanceName":"106"}),makeQuery(id+"F5.opPattern","COPY",FACE,{"derivedFrom":subQ1,"instanceName":"107"}),makeQuery(id+"F5.opPattern","COPY",FACE,{"derivedFrom":subQ1,"instanceName":"108"}),makeQuery(id+"F5.opPattern","COPY",FACE,{"derivedFrom":subQ1,"instanceName":"109"}),makeQuery(id+"F5.opPattern","COPY",FACE,{"derivedFrom":subQ1,"instanceName":"110"}),makeQuery(id+"F5.opPattern","COPY",FACE,{"derivedFrom":subQ1,"instanceName":"111"}),makeQuery(id+"F5.opPattern","COPY",FACE,{"derivedFrom":subQ1,"instanceName":"112"}),makeQuery(id+"F5.opPattern","COPY",FACE,{"derivedFrom":subQ1,"instanceName":"113"}),makeQuery(id+"F5.opPattern","COPY",FACE,{"derivedFrom":subQ1,"instanceName":"114"}),makeQuery(id+"F5.opPattern","COPY",FACE,{"derivedFrom":subQ1,"instanceName":"115"}),makeQuery(id+"F5.opPattern","COPY",FACE,{"derivedFrom":subQ1,"instanceName":"116"}),makeQuery(id+"F5.opPattern","COPY",FACE,{"derivedFrom":subQ1,"instanceName":"117"}),makeQuery(id+"F5.opPattern","COPY",FACE,{"derivedFrom":subQ1,"instanceName":"118"}),makeQuery(id+"F5.opPattern","COPY",FACE,{"derivedFrom":subQ1,"instanceName":"119"}),makeQuery(id+"F5.opPattern","COPY",FACE,{"derivedFrom":subQ1,"instanceName":"120"}),makeQuery(id+"F5.opPattern","COPY",FACE,{"derivedFrom":subQ1,"instanceName":"121"}),makeQuery(id+"F5.opPattern","COPY",FACE,{"derivedFrom":subQ1,"instanceName":"122"}),makeQuery(id+"F5.opPattern","COPY",FACE,{"derivedFrom":subQ1,"instanceName":"123"}),makeQuery(id+"F5.opPattern","COPY",FACE,{"derivedFrom":subQ1,"instanceName":"124"}),makeQuery(id+"F5.opPattern","COPY",FACE,{"derivedFrom":subQ1,"instanceName":"125"}),makeQuery(id+"F5.opPattern","COPY",FACE,{"derivedFrom":subQ1,"instanceName":"126"}),makeQuery(id+"F5.opPattern","COPY",FACE,{"derivedFrom":subQ1,"instanceName":"127"})]});}
            var sketch = newSketch(context, id + "F11", { "sketchPlane" : qUnion([Q0])});
            skCircle(sketch, "E15.0", {"center": v(0, 0) * mm, "radius": 155.58 * mm});
            skCircle(sketch, "E16.0", {"center": v(0, 0) * mm, "radius": 30.23 * mm});
            skSolve(sketch);
        }
        {
            var Q0;
            Q0=qSketchRegion(id+"F11",true);
            extrude(context, id + "F12", {"entities" : qUnion([Q0]), "operationType" : NewBodyOperationType.ADD, "depth" : 17.53 * mm});
        }
    });
